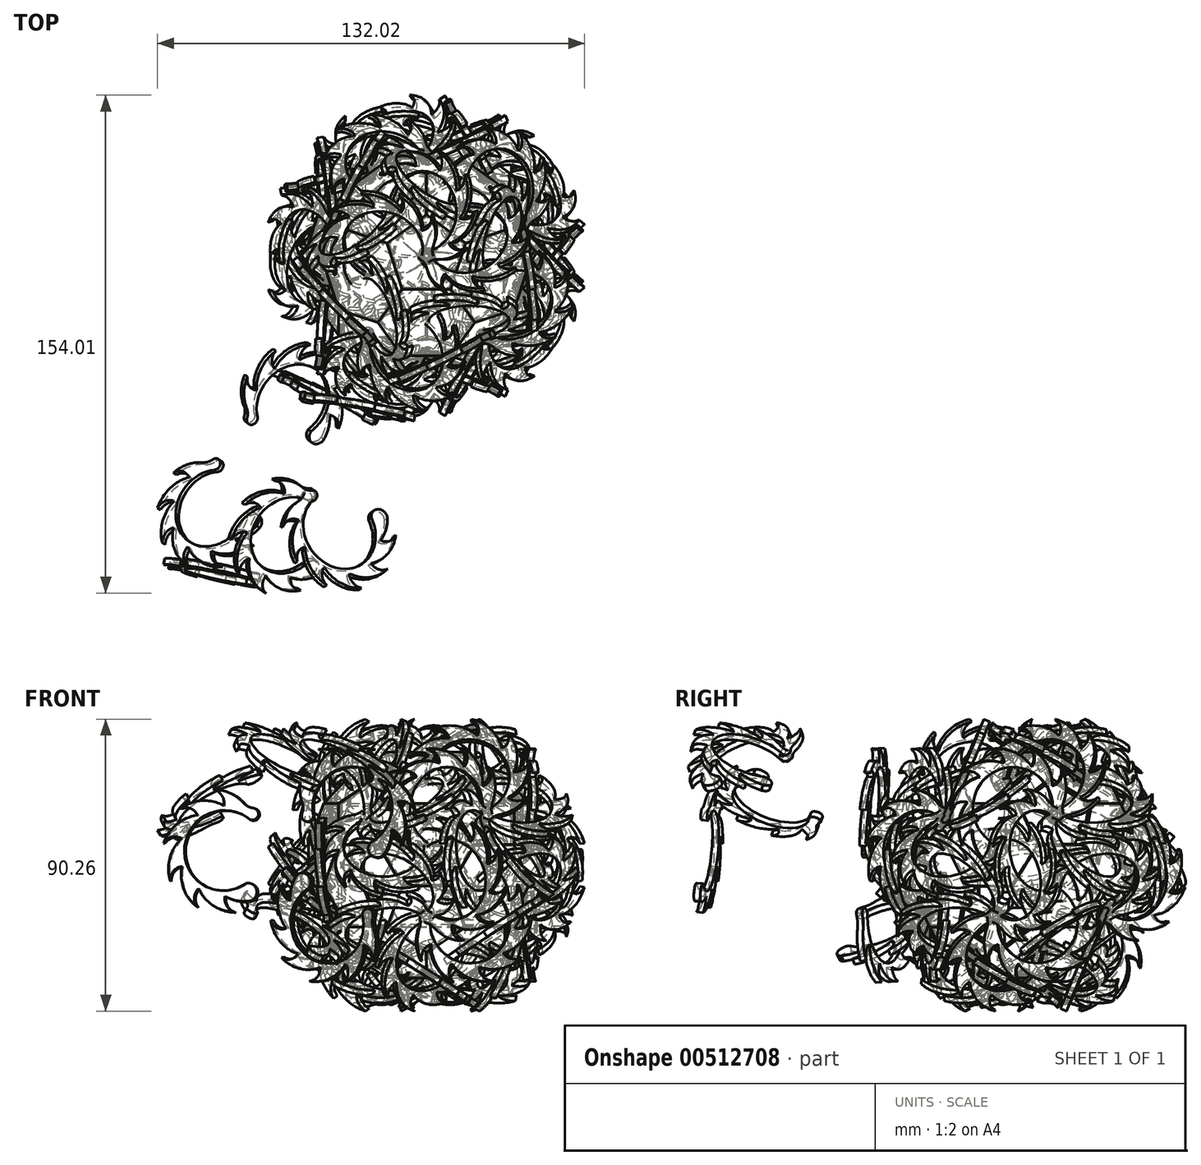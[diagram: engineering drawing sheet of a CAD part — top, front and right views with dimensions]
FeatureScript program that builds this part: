
annotation { "Feature Type Name" : "Feature", "Feature Type Description" : "" }
export const myFeature = defineFeature(function(context is Context, id is Id, definition is map)
    precondition{}
    {
        {
            var Q0;
            Q0=qCreatedBy(makeId("Top.planeOp"),FACE);
            var sketch = newSketch(context, id + "F0", { "sketchPlane" : qUnion([Q0])});
            skCircle(sketch, "E0.cCircle", {"center": v(0, 0) * mm, "radius": 10.32 * mm, "construction": true});
            skLineSegment(sketch, "E0.0", {"start": v(7.5, -10.32) * mm, "end": v(-7.5, -10.32) * mm});
            skLineSegment(sketch, "E0.1", {"start": v(-7.5, -10.32) * mm, "end": v(-12.14, 3.94) * mm});
            skLineSegment(sketch, "E0.2", {"start": v(-12.14, 3.94) * mm, "end": v(0, 12.76) * mm});
            skLineSegment(sketch, "E0.3", {"start": v(0, 12.76) * mm, "end": v(12.14, 3.94) * mm});
            skLineSegment(sketch, "E0.4", {"start": v(12.14, 3.94) * mm, "end": v(7.5, -10.32) * mm});
            skPoint(sketch, "E0.0.midPoint", {"position": v(0, -10.32) * mm});
            skLineSegment(sketch, "E1", {"start": v(0, 12.76) * mm, "end": v(0, -10.32) * mm});
            skSolve(sketch);
        }
        {
            var Q0;
            Q0=qCreatedBy(makeId("Top.planeOp"),FACE);
            var sketch = newSketch(context, id + "F1", { "sketchPlane" : qUnion([Q0])});
            skCircle(sketch, "E2.cCircle", {"center": v(22.17, -7.2) * mm, "radius": 13 * mm, "construction": true});
            skLineSegment(sketch, "E2.0", {"start": v(36.84, -4.09) * mm, "end": v(32.2, -18.35) * mm});
            skLineSegment(sketch, "E2.1", {"start": v(32.2, -18.35) * mm, "end": v(17.54, -21.47) * mm});
            skLineSegment(sketch, "E2.2", {"start": v(17.54, -21.47) * mm, "end": v(7.5, -10.32) * mm});
            skLineSegment(sketch, "E2.3", {"start": v(7.5, -10.32) * mm, "end": v(12.14, 3.94) * mm});
            skLineSegment(sketch, "E2.4", {"start": v(12.14, 3.94) * mm, "end": v(26.8, 7.06) * mm});
            skLineSegment(sketch, "E2.5", {"start": v(26.8, 7.06) * mm, "end": v(36.84, -4.09) * mm});
            skPoint(sketch, "E2.0.midPoint", {"position": v(34.53, -11.22) * mm});
            skSolve(sketch);
        }
        {
            var Q0;
            Q0=makeQuery(id+"F0.imprint","IMPRINT",FACE,{"disambiguationData":[TD([[makeQuery(id+"F0.imprint","IMPRINT",EDGE,{"derivedFrom":sQuery(id+"F0.wireOp",EDGE,"E0.0")}),-1.0]])]});
            extrude(context, id + "F2", {"entities" : qUnion([Q0]), "oppositeDirection" : true, "depth" : 1 * mm});
        }
        {
            var Q0;
            Q0=makeQuery(id+"F1.imprint","IMPRINT",FACE,{"disambiguationData":[TD([[makeQuery(id+"F1.imprint","IMPRINT",EDGE,{"derivedFrom":sQuery(id+"F1.wireOp",EDGE,"E2.0")}),-1.0]])]});
            extrude(context, id + "F3", {"entities" : qUnion([Q0]), "oppositeDirection" : true, "depth" : 1 * mm});
        }
        {
            var Q0;
            Q0=makeQuery(id+"F3.opExtrude","SWEPT_BODY",BODY,{"disambiguationData":[OSD([sQuery(id+"F1.wireOp",EDGE,"E2.0"),sQuery(id+"F1.wireOp",EDGE,"E2.1"),sQuery(id+"F1.wireOp",EDGE,"E2.2"),sQuery(id+"F1.wireOp",EDGE,"E2.3"),sQuery(id+"F1.wireOp",EDGE,"E2.4"),sQuery(id+"F1.wireOp",EDGE,"E2.5")])]});
            var Q1;
            Q1=makeQuery(id+"F2.opExtrude","CAP_EDGE",EDGE,{"disambiguationData":[OSD([sQuery(id+"F0.wireOp",EDGE,"E0.4")])],"isStart":true});
            transform(context, id + "F4", {"entities" : qUnion([Q0]), "transformType" : TransformType.ROTATION, "transformAxis" : qUnion([Q1]), "angle" : 37.38 * degree, "oppositeDirection" : true, "makeCopy" : false});
        }
        {
            var Q0;
            Q0=qCreatedBy(makeId("Right.planeOp"),FACE);
            var sketch = newSketch(context, id + "F5", { "sketchPlane" : qUnion([Q0])});
            skLineSegment(sketch, "E3", {"start": v(0, 0) * mm, "end": v(0, 7.73) * mm});
            skSolve(sketch);
        }
        {
            var Q0;
            Q0=makeQuery(id+"F3.opExtrude","SWEPT_BODY",BODY,{"disambiguationData":[OSD([sQuery(id+"F1.wireOp",EDGE,"E2.0"),sQuery(id+"F1.wireOp",EDGE,"E2.1"),sQuery(id+"F1.wireOp",EDGE,"E2.2"),sQuery(id+"F1.wireOp",EDGE,"E2.3"),sQuery(id+"F1.wireOp",EDGE,"E2.4"),sQuery(id+"F1.wireOp",EDGE,"E2.5")])]});
            var Q1;
            Q1=sQuery(id+"F5.wireOp",EDGE,"E3");
            circularPattern(context, id + "F6", {"entities" : qUnion([Q0]), "axis" : qUnion([Q1]), "angle" : 72 * degree, "instanceCount" : round(5)});
        }
        {
            var Q0;
            Q0=makeQuery(id+"F6.opPattern","COPY",FACE,{"derivedFrom":makeQuery(id+"F3.opExtrude","CAP_FACE",FACE,{"disambiguationData":[OSD([sQuery(id+"F1.wireOp",EDGE,"E2.0"),sQuery(id+"F1.wireOp",EDGE,"E2.1"),sQuery(id+"F1.wireOp",EDGE,"E2.2"),sQuery(id+"F1.wireOp",EDGE,"E2.3"),sQuery(id+"F1.wireOp",EDGE,"E2.4"),sQuery(id+"F1.wireOp",EDGE,"E2.5")])],"isStart":true}),"instanceName":"4"});
            var sketch = newSketch(context, id + "F7", { "sketchPlane" : qUnion([Q0])});
            skLineSegment(sketch, "E4", {"start": v(0, -34.18) * mm, "end": v(0, -8.2) * mm});
            skLineSegment(sketch, "E5", {"start": v(-15, -21.2) * mm, "end": v(15, -21.2) * mm});
            skCircle(sketch, "E6", {"center": v(0, -21.2) * mm, "radius": 3.24 * mm});
            skSolve(sketch);
        }
        {
            var Q0;
            Q0=qCreatedBy(makeId("Right.planeOp"),FACE);
            var sketch = newSketch(context, id + "F8", { "sketchPlane" : qUnion([Q0])});
            skArc(sketch, "E7.0", {"start": v(-1.37, 0) * mm, "mid": v(-18.04, 14.75) * mm, "end": v(-20.04, -7.42) * mm});
            skLineSegment(sketch, "E8", {"start": v(-20.04, -7.42) * mm, "end": v(-24.47, -10.8) * mm});
            skLineSegment(sketch, "E9", {"start": v(-1.37, 0) * mm, "end": v(0, 0) * mm});
            skArc(sketch, "E10", {"start": v(1.07, 1.27) * mm, "mid": v(3.46, 7.37) * mm, "end": v(2.5, 13.85) * mm});
            skArc(sketch, "E11", {"start": v(-0.8, 8.97) * mm, "mid": v(1.84, 10.74) * mm, "end": v(2.5, 13.85) * mm});
            skArc(sketch, "E12.1.0", {"start": v(-0.8, 8.97) * mm, "mid": v(-2.13, 15.94) * mm, "end": v(-6.98, 21.1) * mm});
            skArc(sketch, "E12.1.1", {"start": v(-6.75, 15.32) * mm, "mid": v(-5.72, 18.26) * mm, "end": v(-6.98, 21.1) * mm});
            skArc(sketch, "E12.2.0", {"start": v(-6.75, 15.32) * mm, "mid": v(-11.92, 20.18) * mm, "end": v(-18.89, 21.5) * mm});
            skArc(sketch, "E12.2.1", {"start": v(-15.3, 16.96) * mm, "mid": v(-16.2, 19.94) * mm, "end": v(-18.89, 21.5) * mm});
            skArc(sketch, "E12.3.0", {"start": v(-15.3, 16.96) * mm, "mid": v(-22.34, 17.85) * mm, "end": v(-28.75, 14.83) * mm});
            skArc(sketch, "E12.3.1", {"start": v(-23.18, 13.26) * mm, "mid": v(-25.66, 15.15) * mm, "end": v(-28.75, 14.83) * mm});
            skArc(sketch, "E12.4.0", {"start": v(-23.18, 13.26) * mm, "mid": v(-29.4, 9.84) * mm, "end": v(-32.81, 3.63) * mm});
            skArc(sketch, "E12.4.1", {"start": v(-27.38, 5.64) * mm, "mid": v(-30.5, 5.7) * mm, "end": v(-32.81, 3.63) * mm});
            skArc(sketch, "E12.5.0", {"start": v(-27.38, 5.64) * mm, "mid": v(-30.4, -0.78) * mm, "end": v(-29.51, -7.81) * mm});
            skArc(sketch, "E12.5.1", {"start": v(-26.3, -3) * mm, "mid": v(-28.86, -4.77) * mm, "end": v(-29.51, -7.81) * mm});
            skArc(sketch, "E12.6.0", {"start": v(-26.3, -3) * mm, "mid": v(-26.03, -7.06) * mm, "end": v(-24.49, -10.82) * mm});
            skArc(sketch, "E13", {"start": v(-24.49, -10.82) * mm, "mid": v(-20.56, -11.35) * mm, "end": v(-20.04, -7.42) * mm});
            skArc(sketch, "E14", {"start": v(-1.37, 0) * mm, "mid": v(1.27, -2.11) * mm, "end": v(1.07, 1.27) * mm});
            skSolve(sketch);
        }
        {
            var Q0;
            {var subQ2=sQuery(id+"F8.wireOp",EDGE,"E7.0");Q0=makeQuery(id+"F8.imprint","IMPRINT",FACE,{"disambiguationData":[TD([[makeQuery(id+"F8.imprint","IMPRINT",EDGE,{"derivedFrom":subQ2}),-1.0]])]});}
            extrude(context, id + "F9", {"entities" : qUnion([Q0]), "oppositeDirection" : true, "depth" : 2 * mm});
        }
        {
            var Q0;
            Q0=makeQuery(id+"F9.opExtrude","SWEPT_EDGE",EDGE,{"disambiguationData":[OSD([sQuery(id+"F8.wireOp",EDGE,"E10"),sQuery(id+"F8.wireOp",EDGE,"E14")])]});
            fillet(context, id + "F10", {"entities" : qUnion([Q0]), "radius" : 5.46 * mm, "tangentPropagation" : true, "allowEdgeOverflow" : false});
        }
        {
            var Q0;
            Q0=qCreatedBy(makeId("Right.planeOp"),FACE);
            var sketch = newSketch(context, id + "F11", { "sketchPlane" : qUnion([Q0])});
            skLineSegment(sketch, "E15", {"start": v(0, 0) * mm, "end": v(-20.65, -7.89) * mm});
            skLineSegment(sketch, "E16", {"start": v(0, 0) * mm, "end": v(0, 28.42) * mm});
            skSolve(sketch);
        }
        {
            var Q0;
            Q0=makeQuery(id+"F9.opExtrude","SWEPT_BODY",BODY,{"disambiguationData":[OSD([sQuery(id+"F8.wireOp",EDGE,"003f2e54-bd62-4f0b-a98e-8c36e71e2cf6"),sQuery(id+"F8.wireOp",EDGE,"8c729305-40a1-49fa-b790-4b99a3909bb6"),sQuery(id+"F8.wireOp",EDGE,"862a2a8f-3db7-4421-9c69-6ab2f53c4c24.1.0"),sQuery(id+"F8.wireOp",EDGE,"862a2a8f-3db7-4421-9c69-6ab2f53c4c24.1.1"),sQuery(id+"F8.wireOp",EDGE,"862a2a8f-3db7-4421-9c69-6ab2f53c4c24.2.0"),sQuery(id+"F8.wireOp",EDGE,"862a2a8f-3db7-4421-9c69-6ab2f53c4c24.2.1"),sQuery(id+"F8.wireOp",EDGE,"862a2a8f-3db7-4421-9c69-6ab2f53c4c24.3.0"),sQuery(id+"F8.wireOp",EDGE,"862a2a8f-3db7-4421-9c69-6ab2f53c4c24.3.1"),sQuery(id+"F8.wireOp",EDGE,"862a2a8f-3db7-4421-9c69-6ab2f53c4c24.4.0"),sQuery(id+"F8.wireOp",EDGE,"862a2a8f-3db7-4421-9c69-6ab2f53c4c24.4.1"),sQuery(id+"F8.wireOp",EDGE,"862a2a8f-3db7-4421-9c69-6ab2f53c4c24.5.0"),sQuery(id+"F8.wireOp",EDGE,"E7.0"),sQuery(id+"F8.wireOp",EDGE,"E8"),sQuery(id+"F8.wireOp",EDGE,"E9")])]});
            var Q1;
            Q1=sQuery(id+"F11.wireOp",EDGE,"E15");
            transform(context, id + "F12", {"entities" : qUnion([Q0]), "transformType" : TransformType.ROTATION, "transformAxis" : qUnion([Q1]), "angle" : 65 * degree, "makeCopy" : false});
        }
        {
            var Q0;
            Q0=makeQuery(id+"F9.opExtrude","SWEPT_BODY",BODY,{"disambiguationData":[OSD([sQuery(id+"F8.wireOp",EDGE,"003f2e54-bd62-4f0b-a98e-8c36e71e2cf6"),sQuery(id+"F8.wireOp",EDGE,"8c729305-40a1-49fa-b790-4b99a3909bb6"),sQuery(id+"F8.wireOp",EDGE,"862a2a8f-3db7-4421-9c69-6ab2f53c4c24.1.0"),sQuery(id+"F8.wireOp",EDGE,"862a2a8f-3db7-4421-9c69-6ab2f53c4c24.1.1"),sQuery(id+"F8.wireOp",EDGE,"862a2a8f-3db7-4421-9c69-6ab2f53c4c24.2.0"),sQuery(id+"F8.wireOp",EDGE,"862a2a8f-3db7-4421-9c69-6ab2f53c4c24.2.1"),sQuery(id+"F8.wireOp",EDGE,"862a2a8f-3db7-4421-9c69-6ab2f53c4c24.3.0"),sQuery(id+"F8.wireOp",EDGE,"862a2a8f-3db7-4421-9c69-6ab2f53c4c24.3.1"),sQuery(id+"F8.wireOp",EDGE,"862a2a8f-3db7-4421-9c69-6ab2f53c4c24.4.0"),sQuery(id+"F8.wireOp",EDGE,"862a2a8f-3db7-4421-9c69-6ab2f53c4c24.4.1"),sQuery(id+"F8.wireOp",EDGE,"862a2a8f-3db7-4421-9c69-6ab2f53c4c24.5.0"),sQuery(id+"F8.wireOp",EDGE,"E7.0"),sQuery(id+"F8.wireOp",EDGE,"E8"),sQuery(id+"F8.wireOp",EDGE,"E9")])]});
            var Q1;
            Q1=sQuery(id+"F11.wireOp",EDGE,"E16");
            circularPattern(context, id + "F13", {"entities" : qUnion([Q0]), "axis" : qUnion([Q1]), "angle" : 72 * degree, "instanceCount" : round(5)});
        }
        {
            var Q0;
            Q0=qCreatedBy(makeId("Right.planeOp"),FACE);
            var sketch = newSketch(context, id + "F14", { "sketchPlane" : qUnion([Q0])});
            skLineSegment(sketch, "E17.0", {"start": v(-30.97, -15.77) * mm, "end": v(-10.32, 0) * mm});
            skLineSegment(sketch, "E18", {"start": v(-20.65, -7.89) * mm, "end": v(-30.05, 4.42) * mm});
            skSolve(sketch);
        }
        {
            var Q0;
            Q0=makeQuery(id+"F9.opExtrude","SWEPT_BODY",BODY,{"disambiguationData":[OSD([sQuery(id+"F8.wireOp",EDGE,"003f2e54-bd62-4f0b-a98e-8c36e71e2cf6"),sQuery(id+"F8.wireOp",EDGE,"8c729305-40a1-49fa-b790-4b99a3909bb6"),sQuery(id+"F8.wireOp",EDGE,"862a2a8f-3db7-4421-9c69-6ab2f53c4c24.1.0"),sQuery(id+"F8.wireOp",EDGE,"862a2a8f-3db7-4421-9c69-6ab2f53c4c24.1.1"),sQuery(id+"F8.wireOp",EDGE,"862a2a8f-3db7-4421-9c69-6ab2f53c4c24.2.0"),sQuery(id+"F8.wireOp",EDGE,"862a2a8f-3db7-4421-9c69-6ab2f53c4c24.2.1"),sQuery(id+"F8.wireOp",EDGE,"862a2a8f-3db7-4421-9c69-6ab2f53c4c24.3.0"),sQuery(id+"F8.wireOp",EDGE,"862a2a8f-3db7-4421-9c69-6ab2f53c4c24.3.1"),sQuery(id+"F8.wireOp",EDGE,"862a2a8f-3db7-4421-9c69-6ab2f53c4c24.4.0"),sQuery(id+"F8.wireOp",EDGE,"862a2a8f-3db7-4421-9c69-6ab2f53c4c24.4.1"),sQuery(id+"F8.wireOp",EDGE,"862a2a8f-3db7-4421-9c69-6ab2f53c4c24.5.0"),sQuery(id+"F8.wireOp",EDGE,"E7.0"),sQuery(id+"F8.wireOp",EDGE,"E8"),sQuery(id+"F8.wireOp",EDGE,"E9")])]});
            var Q1;
            Q1=sQuery(id+"F14.wireOp",EDGE,"E18");
            circularPattern(context, id + "F15", {"entities" : qUnion([Q0]), "axis" : qUnion([Q1]), "angle" : 120 * degree, "instanceCount" : round(3)});
        }
        {
            var Q0;
            Q0=makeQuery(id+"F15.opPattern","COPY",BODY,{"derivedFrom":makeQuery(id+"F9.opExtrude","SWEPT_BODY",BODY,{"disambiguationData":[OSD([sQuery(id+"F8.wireOp",EDGE,"E7.0"),sQuery(id+"F8.wireOp",EDGE,"E10"),sQuery(id+"F8.wireOp",EDGE,"E11"),sQuery(id+"F8.wireOp",EDGE,"E12.1.0"),sQuery(id+"F8.wireOp",EDGE,"E12.1.1"),sQuery(id+"F8.wireOp",EDGE,"E12.2.0"),sQuery(id+"F8.wireOp",EDGE,"E12.2.1"),sQuery(id+"F8.wireOp",EDGE,"E12.3.0"),sQuery(id+"F8.wireOp",EDGE,"E12.3.1"),sQuery(id+"F8.wireOp",EDGE,"E12.4.0"),sQuery(id+"F8.wireOp",EDGE,"E12.4.1"),sQuery(id+"F8.wireOp",EDGE,"E12.5.0"),sQuery(id+"F8.wireOp",EDGE,"E12.5.1"),sQuery(id+"F8.wireOp",EDGE,"E12.6.0"),sQuery(id+"F8.wireOp",EDGE,"E13"),sQuery(id+"F8.wireOp",EDGE,"E14")])]}),"instanceName":"2"});
            var Q1;
            Q1=makeQuery(id+"F15.opPattern","COPY",BODY,{"derivedFrom":makeQuery(id+"F9.opExtrude","SWEPT_BODY",BODY,{"disambiguationData":[OSD([sQuery(id+"F8.wireOp",EDGE,"E7.0"),sQuery(id+"F8.wireOp",EDGE,"E10"),sQuery(id+"F8.wireOp",EDGE,"E11"),sQuery(id+"F8.wireOp",EDGE,"E12.1.0"),sQuery(id+"F8.wireOp",EDGE,"E12.1.1"),sQuery(id+"F8.wireOp",EDGE,"E12.2.0"),sQuery(id+"F8.wireOp",EDGE,"E12.2.1"),sQuery(id+"F8.wireOp",EDGE,"E12.3.0"),sQuery(id+"F8.wireOp",EDGE,"E12.3.1"),sQuery(id+"F8.wireOp",EDGE,"E12.4.0"),sQuery(id+"F8.wireOp",EDGE,"E12.4.1"),sQuery(id+"F8.wireOp",EDGE,"E12.5.0"),sQuery(id+"F8.wireOp",EDGE,"E12.5.1"),sQuery(id+"F8.wireOp",EDGE,"E12.6.0"),sQuery(id+"F8.wireOp",EDGE,"E13"),sQuery(id+"F8.wireOp",EDGE,"E14")])]}),"instanceName":"1"});
            var Q2;
            Q2=sQuery(id+"F11.wireOp",EDGE,"E16");
            circularPattern(context, id + "F16", {"entities" : qUnion([Q0, Q1]), "axis" : qUnion([Q2]), "angle" : 72 * degree, "instanceCount" : round(5)});
        }
        {
            var Q0;
            Q0=makeQuery(id+"F3.opExtrude","SWEPT_BODY",BODY,{"disambiguationData":[OSD([sQuery(id+"F1.wireOp",EDGE,"E2.0"),sQuery(id+"F1.wireOp",EDGE,"E2.1"),sQuery(id+"F1.wireOp",EDGE,"E2.2"),sQuery(id+"F1.wireOp",EDGE,"E2.3"),sQuery(id+"F1.wireOp",EDGE,"E2.4"),sQuery(id+"F1.wireOp",EDGE,"E2.5")])]});
            var Q1;
            Q1=makeQuery(id+"F16.opPattern","COPY",BODY,{"derivedFrom":makeQuery(id+"F15.opPattern","COPY",BODY,{"derivedFrom":makeQuery(id+"F9.opExtrude","SWEPT_BODY",BODY,{"disambiguationData":[OSD([sQuery(id+"F8.wireOp",EDGE,"E7.0"),sQuery(id+"F8.wireOp",EDGE,"E10"),sQuery(id+"F8.wireOp",EDGE,"E11"),sQuery(id+"F8.wireOp",EDGE,"E12.1.0"),sQuery(id+"F8.wireOp",EDGE,"E12.1.1"),sQuery(id+"F8.wireOp",EDGE,"E12.2.0"),sQuery(id+"F8.wireOp",EDGE,"E12.2.1"),sQuery(id+"F8.wireOp",EDGE,"E12.3.0"),sQuery(id+"F8.wireOp",EDGE,"E12.3.1"),sQuery(id+"F8.wireOp",EDGE,"E12.4.0"),sQuery(id+"F8.wireOp",EDGE,"E12.4.1"),sQuery(id+"F8.wireOp",EDGE,"E12.5.0"),sQuery(id+"F8.wireOp",EDGE,"E12.5.1"),sQuery(id+"F8.wireOp",EDGE,"E12.6.0"),sQuery(id+"F8.wireOp",EDGE,"E13"),sQuery(id+"F8.wireOp",EDGE,"E14")])]}),"instanceName":"1"}),"instanceName":"1"});
            var Q2;
            Q2=makeQuery(id+"F13.opPattern","COPY",BODY,{"derivedFrom":makeQuery(id+"F9.opExtrude","SWEPT_BODY",BODY,{"disambiguationData":[OSD([sQuery(id+"F8.wireOp",EDGE,"E7.0"),sQuery(id+"F8.wireOp",EDGE,"E10"),sQuery(id+"F8.wireOp",EDGE,"E11"),sQuery(id+"F8.wireOp",EDGE,"E12.1.0"),sQuery(id+"F8.wireOp",EDGE,"E12.1.1"),sQuery(id+"F8.wireOp",EDGE,"E12.2.0"),sQuery(id+"F8.wireOp",EDGE,"E12.2.1"),sQuery(id+"F8.wireOp",EDGE,"E12.3.0"),sQuery(id+"F8.wireOp",EDGE,"E12.3.1"),sQuery(id+"F8.wireOp",EDGE,"E12.4.0"),sQuery(id+"F8.wireOp",EDGE,"E12.4.1"),sQuery(id+"F8.wireOp",EDGE,"E12.5.0"),sQuery(id+"F8.wireOp",EDGE,"E12.5.1"),sQuery(id+"F8.wireOp",EDGE,"E12.6.0"),sQuery(id+"F8.wireOp",EDGE,"E13"),sQuery(id+"F8.wireOp",EDGE,"E14")])]}),"instanceName":"1"});
            var Q3;
            Q3=makeQuery(id+"F16.opPattern","COPY",BODY,{"derivedFrom":makeQuery(id+"F15.opPattern","COPY",BODY,{"derivedFrom":makeQuery(id+"F9.opExtrude","SWEPT_BODY",BODY,{"disambiguationData":[OSD([sQuery(id+"F8.wireOp",EDGE,"E7.0"),sQuery(id+"F8.wireOp",EDGE,"E10"),sQuery(id+"F8.wireOp",EDGE,"E11"),sQuery(id+"F8.wireOp",EDGE,"E12.1.0"),sQuery(id+"F8.wireOp",EDGE,"E12.1.1"),sQuery(id+"F8.wireOp",EDGE,"E12.2.0"),sQuery(id+"F8.wireOp",EDGE,"E12.2.1"),sQuery(id+"F8.wireOp",EDGE,"E12.3.0"),sQuery(id+"F8.wireOp",EDGE,"E12.3.1"),sQuery(id+"F8.wireOp",EDGE,"E12.4.0"),sQuery(id+"F8.wireOp",EDGE,"E12.4.1"),sQuery(id+"F8.wireOp",EDGE,"E12.5.0"),sQuery(id+"F8.wireOp",EDGE,"E12.5.1"),sQuery(id+"F8.wireOp",EDGE,"E12.6.0"),sQuery(id+"F8.wireOp",EDGE,"E13"),sQuery(id+"F8.wireOp",EDGE,"E14")])]}),"instanceName":"2"}),"instanceName":"1"});
            var Q4;
            Q4=sQuery(id+"F14.wireOp",EDGE,"E18");
            circularPattern(context, id + "F17", {"entities" : qUnion([Q0, Q1, Q2, Q3]), "axis" : qUnion([Q4]), "angle" : 120 * degree, "instanceCount" : 2, "oppositeDirection" : true});
        }
        {
            var Q0;
            Q0=makeQuery(id+"F2.opExtrude","SWEPT_BODY",BODY,{"disambiguationData":[OSD([sQuery(id+"F0.wireOp",EDGE,"E0.0"),sQuery(id+"F0.wireOp",EDGE,"E0.1"),sQuery(id+"F0.wireOp",EDGE,"E0.2"),sQuery(id+"F0.wireOp",EDGE,"E0.3"),sQuery(id+"F0.wireOp",EDGE,"E0.4")])]});
            var Q1;
            Q1=makeQuery(id+"F13.opPattern","COPY",BODY,{"derivedFrom":makeQuery(id+"F9.opExtrude","SWEPT_BODY",BODY,{"disambiguationData":[OSD([sQuery(id+"F8.wireOp",EDGE,"E7.0"),sQuery(id+"F8.wireOp",EDGE,"E10"),sQuery(id+"F8.wireOp",EDGE,"E11"),sQuery(id+"F8.wireOp",EDGE,"E12.1.0"),sQuery(id+"F8.wireOp",EDGE,"E12.1.1"),sQuery(id+"F8.wireOp",EDGE,"E12.2.0"),sQuery(id+"F8.wireOp",EDGE,"E12.2.1"),sQuery(id+"F8.wireOp",EDGE,"E12.3.0"),sQuery(id+"F8.wireOp",EDGE,"E12.3.1"),sQuery(id+"F8.wireOp",EDGE,"E12.4.0"),sQuery(id+"F8.wireOp",EDGE,"E12.4.1"),sQuery(id+"F8.wireOp",EDGE,"E12.5.0"),sQuery(id+"F8.wireOp",EDGE,"E12.5.1"),sQuery(id+"F8.wireOp",EDGE,"E12.6.0"),sQuery(id+"F8.wireOp",EDGE,"E13"),sQuery(id+"F8.wireOp",EDGE,"E14")])]}),"instanceName":"2"});
            var Q2;
            Q2=makeQuery(id+"F13.opPattern","COPY",BODY,{"derivedFrom":makeQuery(id+"F9.opExtrude","SWEPT_BODY",BODY,{"disambiguationData":[OSD([sQuery(id+"F8.wireOp",EDGE,"E7.0"),sQuery(id+"F8.wireOp",EDGE,"E10"),sQuery(id+"F8.wireOp",EDGE,"E11"),sQuery(id+"F8.wireOp",EDGE,"E12.1.0"),sQuery(id+"F8.wireOp",EDGE,"E12.1.1"),sQuery(id+"F8.wireOp",EDGE,"E12.2.0"),sQuery(id+"F8.wireOp",EDGE,"E12.2.1"),sQuery(id+"F8.wireOp",EDGE,"E12.3.0"),sQuery(id+"F8.wireOp",EDGE,"E12.3.1"),sQuery(id+"F8.wireOp",EDGE,"E12.4.0"),sQuery(id+"F8.wireOp",EDGE,"E12.4.1"),sQuery(id+"F8.wireOp",EDGE,"E12.5.0"),sQuery(id+"F8.wireOp",EDGE,"E12.5.1"),sQuery(id+"F8.wireOp",EDGE,"E12.6.0"),sQuery(id+"F8.wireOp",EDGE,"E13"),sQuery(id+"F8.wireOp",EDGE,"E14")])]}),"instanceName":"3"});
            var Q3;
            Q3=sQuery(id+"F14.wireOp",EDGE,"E18");
            circularPattern(context, id + "F18", {"entities" : qUnion([Q0, Q1, Q2]), "axis" : qUnion([Q3]), "angle" : 120 * degree, "instanceCount" : round(3)});
        }
        {
            var Q0;
            Q0=makeQuery(id+"F18.opPattern","COPY",FACE,{"derivedFrom":makeQuery(id+"F2.opExtrude","CAP_FACE",FACE,{"disambiguationData":[OSD([sQuery(id+"F0.wireOp",EDGE,"E0.0"),sQuery(id+"F0.wireOp",EDGE,"E0.1"),sQuery(id+"F0.wireOp",EDGE,"E0.2"),sQuery(id+"F0.wireOp",EDGE,"E0.3"),sQuery(id+"F0.wireOp",EDGE,"E0.4")])],"isStart":true}),"instanceName":"1"});
            var sketch = newSketch(context, id + "F19", { "sketchPlane" : qUnion([Q0])});
            skLineSegment(sketch, "E19", {"start": v(-1.3, -23.63) * mm, "end": v(-19.97, -37.2) * mm});
            skLineSegment(sketch, "E20", {"start": v(-19.97, -22.2) * mm, "end": v(-1.3, -35.77) * mm});
            skSolve(sketch);
        }
        {
            var Q0;
            Q0=sQuery(id+"F19.wireOp",VERTEX,"E19.end");
            var Q1;
            Q1=sQuery(id+"F19.wireOp",VERTEX,"E19.start");
            var Q2;
            Q2=sQuery(id+"F14.wireOp",VERTEX,"E18.end");
            cPlane(context, id + "F20", {"entities" : qUnion([Q0, Q1, Q2]), "cplaneType" : CPlaneType.THREE_POINT, "offset" : 150 * mm, "width" : 150 * mm, "height" : 150 * mm});
        }
        {
            var Q0;
            Q0=qCreatedBy(id+"F20.planeOp",FACE);
            var sketch = newSketch(context, id + "F21", { "sketchPlane" : qUnion([Q0])});
            skLineSegment(sketch, "E21.0", {"start": v(23.59, 6.27) * mm, "end": v(41.93, -7.75) * mm});
            skLineSegment(sketch, "E21.1", {"start": v(34.92, -2.4) * mm, "end": v(29.26, 1.94) * mm});
            skLineSegment(sketch, "E22", {"start": v(31.8, 0) * mm, "end": v(33.22, 1.87) * mm});
            skLineSegment(sketch, "E23", {"start": v(33.22, 1.87) * mm, "end": v(37.58, 7.58) * mm});
            skSolve(sketch);
        }
        {
            var Q0;
            Q0=makeQuery(id+"F17.opPattern","COPY",BODY,{"derivedFrom":makeQuery(id+"F3.opExtrude","SWEPT_BODY",BODY,{"disambiguationData":[OSD([sQuery(id+"F1.wireOp",EDGE,"E2.0"),sQuery(id+"F1.wireOp",EDGE,"E2.1"),sQuery(id+"F1.wireOp",EDGE,"E2.2"),sQuery(id+"F1.wireOp",EDGE,"E2.3"),sQuery(id+"F1.wireOp",EDGE,"E2.4"),sQuery(id+"F1.wireOp",EDGE,"E2.5")])]}),"instanceName":"1"});
            var Q1;
            Q1=makeQuery(id+"F17.opPattern","COPY",BODY,{"derivedFrom":makeQuery(id+"F13.opPattern","COPY",BODY,{"derivedFrom":makeQuery(id+"F9.opExtrude","SWEPT_BODY",BODY,{"disambiguationData":[OSD([sQuery(id+"F8.wireOp",EDGE,"E7.0"),sQuery(id+"F8.wireOp",EDGE,"E10"),sQuery(id+"F8.wireOp",EDGE,"E11"),sQuery(id+"F8.wireOp",EDGE,"E12.1.0"),sQuery(id+"F8.wireOp",EDGE,"E12.1.1"),sQuery(id+"F8.wireOp",EDGE,"E12.2.0"),sQuery(id+"F8.wireOp",EDGE,"E12.2.1"),sQuery(id+"F8.wireOp",EDGE,"E12.3.0"),sQuery(id+"F8.wireOp",EDGE,"E12.3.1"),sQuery(id+"F8.wireOp",EDGE,"E12.4.0"),sQuery(id+"F8.wireOp",EDGE,"E12.4.1"),sQuery(id+"F8.wireOp",EDGE,"E12.5.0"),sQuery(id+"F8.wireOp",EDGE,"E12.5.1"),sQuery(id+"F8.wireOp",EDGE,"E12.6.0"),sQuery(id+"F8.wireOp",EDGE,"E13"),sQuery(id+"F8.wireOp",EDGE,"E14")])]}),"instanceName":"1"}),"instanceName":"1"});
            var Q2;
            Q2=makeQuery(id+"F17.opPattern","COPY",BODY,{"derivedFrom":makeQuery(id+"F16.opPattern","COPY",BODY,{"derivedFrom":makeQuery(id+"F15.opPattern","COPY",BODY,{"derivedFrom":makeQuery(id+"F9.opExtrude","SWEPT_BODY",BODY,{"disambiguationData":[OSD([sQuery(id+"F8.wireOp",EDGE,"E7.0"),sQuery(id+"F8.wireOp",EDGE,"E10"),sQuery(id+"F8.wireOp",EDGE,"E11"),sQuery(id+"F8.wireOp",EDGE,"E12.1.0"),sQuery(id+"F8.wireOp",EDGE,"E12.1.1"),sQuery(id+"F8.wireOp",EDGE,"E12.2.0"),sQuery(id+"F8.wireOp",EDGE,"E12.2.1"),sQuery(id+"F8.wireOp",EDGE,"E12.3.0"),sQuery(id+"F8.wireOp",EDGE,"E12.3.1"),sQuery(id+"F8.wireOp",EDGE,"E12.4.0"),sQuery(id+"F8.wireOp",EDGE,"E12.4.1"),sQuery(id+"F8.wireOp",EDGE,"E12.5.0"),sQuery(id+"F8.wireOp",EDGE,"E12.5.1"),sQuery(id+"F8.wireOp",EDGE,"E12.6.0"),sQuery(id+"F8.wireOp",EDGE,"E13"),sQuery(id+"F8.wireOp",EDGE,"E14")])]}),"instanceName":"2"}),"instanceName":"1"}),"instanceName":"1"});
            var Q3;
            Q3=makeQuery(id+"F17.opPattern","COPY",BODY,{"derivedFrom":makeQuery(id+"F16.opPattern","COPY",BODY,{"derivedFrom":makeQuery(id+"F15.opPattern","COPY",BODY,{"derivedFrom":makeQuery(id+"F9.opExtrude","SWEPT_BODY",BODY,{"disambiguationData":[OSD([sQuery(id+"F8.wireOp",EDGE,"E7.0"),sQuery(id+"F8.wireOp",EDGE,"E10"),sQuery(id+"F8.wireOp",EDGE,"E11"),sQuery(id+"F8.wireOp",EDGE,"E12.1.0"),sQuery(id+"F8.wireOp",EDGE,"E12.1.1"),sQuery(id+"F8.wireOp",EDGE,"E12.2.0"),sQuery(id+"F8.wireOp",EDGE,"E12.2.1"),sQuery(id+"F8.wireOp",EDGE,"E12.3.0"),sQuery(id+"F8.wireOp",EDGE,"E12.3.1"),sQuery(id+"F8.wireOp",EDGE,"E12.4.0"),sQuery(id+"F8.wireOp",EDGE,"E12.4.1"),sQuery(id+"F8.wireOp",EDGE,"E12.5.0"),sQuery(id+"F8.wireOp",EDGE,"E12.5.1"),sQuery(id+"F8.wireOp",EDGE,"E12.6.0"),sQuery(id+"F8.wireOp",EDGE,"E13"),sQuery(id+"F8.wireOp",EDGE,"E14")])]}),"instanceName":"1"}),"instanceName":"1"}),"instanceName":"1"});
            var Q4;
            Q4=sQuery(id+"F21.wireOp",EDGE,"E22");
            circularPattern(context, id + "F22", {"entities" : qUnion([Q0, Q1, Q2, Q3]), "axis" : qUnion([Q4]), "angle" : 72 * degree, "instanceCount" : round(3), "oppositeDirection" : true});
        }
        {
            var Q0;
            Q0=makeQuery(id+"F18.opPattern","COPY",FACE,{"derivedFrom":makeQuery(id+"F2.opExtrude","CAP_FACE",FACE,{"disambiguationData":[OSD([sQuery(id+"F0.wireOp",EDGE,"E0.0"),sQuery(id+"F0.wireOp",EDGE,"E0.1"),sQuery(id+"F0.wireOp",EDGE,"E0.2"),sQuery(id+"F0.wireOp",EDGE,"E0.3"),sQuery(id+"F0.wireOp",EDGE,"E0.4")])],"isStart":true}),"instanceName":"2"});
            var sketch = newSketch(context, id + "F23", { "sketchPlane" : qUnion([Q0])});
            skLineSegment(sketch, "E24", {"start": v(1.3, -23.63) * mm, "end": v(19.97, -37.2) * mm});
            skLineSegment(sketch, "E25", {"start": v(5.7, -41.83) * mm, "end": v(12.84, -19.88) * mm});
            skSolve(sketch);
        }
        {
            var Q0;
            Q0=sQuery(id+"F23.wireOp",VERTEX,"E24.end");
            var Q1;
            Q1=sQuery(id+"F23.wireOp",VERTEX,"E24.start");
            var Q2;
            Q2=sQuery(id+"F14.wireOp",VERTEX,"E18.end");
            cPlane(context, id + "F24", {"entities" : qUnion([Q0, Q1, Q2]), "cplaneType" : CPlaneType.THREE_POINT, "offset" : 150 * mm, "width" : 150 * mm, "height" : 150 * mm});
        }
        {
            var Q0;
            Q0=qCreatedBy(id+"F24.planeOp",FACE);
            var sketch = newSketch(context, id + "F25", { "sketchPlane" : qUnion([Q0])});
            skLineSegment(sketch, "E26.0", {"start": v(23.59, 6.27) * mm, "end": v(41.93, -7.75) * mm});
            skLineSegment(sketch, "E26.1", {"start": v(34.92, -2.4) * mm, "end": v(29.26, 1.94) * mm});
            skLineSegment(sketch, "E27", {"start": v(31.8, 0) * mm, "end": v(36.23, 5.8) * mm});
            skSolve(sketch);
        }
        {
            var Q0;
            Q0=makeQuery(id+"F3.opExtrude","SWEPT_BODY",BODY,{"disambiguationData":[OSD([sQuery(id+"F1.wireOp",EDGE,"E2.0"),sQuery(id+"F1.wireOp",EDGE,"E2.1"),sQuery(id+"F1.wireOp",EDGE,"E2.2"),sQuery(id+"F1.wireOp",EDGE,"E2.3"),sQuery(id+"F1.wireOp",EDGE,"E2.4"),sQuery(id+"F1.wireOp",EDGE,"E2.5")])]});
            var Q1;
            Q1=makeQuery(id+"F16.opPattern","COPY",BODY,{"derivedFrom":makeQuery(id+"F15.opPattern","COPY",BODY,{"derivedFrom":makeQuery(id+"F9.opExtrude","SWEPT_BODY",BODY,{"disambiguationData":[OSD([sQuery(id+"F8.wireOp",EDGE,"E7.0"),sQuery(id+"F8.wireOp",EDGE,"E10"),sQuery(id+"F8.wireOp",EDGE,"E11"),sQuery(id+"F8.wireOp",EDGE,"E12.1.0"),sQuery(id+"F8.wireOp",EDGE,"E12.1.1"),sQuery(id+"F8.wireOp",EDGE,"E12.2.0"),sQuery(id+"F8.wireOp",EDGE,"E12.2.1"),sQuery(id+"F8.wireOp",EDGE,"E12.3.0"),sQuery(id+"F8.wireOp",EDGE,"E12.3.1"),sQuery(id+"F8.wireOp",EDGE,"E12.4.0"),sQuery(id+"F8.wireOp",EDGE,"E12.4.1"),sQuery(id+"F8.wireOp",EDGE,"E12.5.0"),sQuery(id+"F8.wireOp",EDGE,"E12.5.1"),sQuery(id+"F8.wireOp",EDGE,"E12.6.0"),sQuery(id+"F8.wireOp",EDGE,"E13"),sQuery(id+"F8.wireOp",EDGE,"E14")])]}),"instanceName":"2"}),"instanceName":"1"});
            var Q2;
            Q2=makeQuery(id+"F13.opPattern","COPY",BODY,{"derivedFrom":makeQuery(id+"F9.opExtrude","SWEPT_BODY",BODY,{"disambiguationData":[OSD([sQuery(id+"F8.wireOp",EDGE,"E7.0"),sQuery(id+"F8.wireOp",EDGE,"E10"),sQuery(id+"F8.wireOp",EDGE,"E11"),sQuery(id+"F8.wireOp",EDGE,"E12.1.0"),sQuery(id+"F8.wireOp",EDGE,"E12.1.1"),sQuery(id+"F8.wireOp",EDGE,"E12.2.0"),sQuery(id+"F8.wireOp",EDGE,"E12.2.1"),sQuery(id+"F8.wireOp",EDGE,"E12.3.0"),sQuery(id+"F8.wireOp",EDGE,"E12.3.1"),sQuery(id+"F8.wireOp",EDGE,"E12.4.0"),sQuery(id+"F8.wireOp",EDGE,"E12.4.1"),sQuery(id+"F8.wireOp",EDGE,"E12.5.0"),sQuery(id+"F8.wireOp",EDGE,"E12.5.1"),sQuery(id+"F8.wireOp",EDGE,"E12.6.0"),sQuery(id+"F8.wireOp",EDGE,"E13"),sQuery(id+"F8.wireOp",EDGE,"E14")])]}),"instanceName":"1"});
            var Q3;
            Q3=makeQuery(id+"F16.opPattern","COPY",BODY,{"derivedFrom":makeQuery(id+"F15.opPattern","COPY",BODY,{"derivedFrom":makeQuery(id+"F9.opExtrude","SWEPT_BODY",BODY,{"disambiguationData":[OSD([sQuery(id+"F8.wireOp",EDGE,"E7.0"),sQuery(id+"F8.wireOp",EDGE,"E10"),sQuery(id+"F8.wireOp",EDGE,"E11"),sQuery(id+"F8.wireOp",EDGE,"E12.1.0"),sQuery(id+"F8.wireOp",EDGE,"E12.1.1"),sQuery(id+"F8.wireOp",EDGE,"E12.2.0"),sQuery(id+"F8.wireOp",EDGE,"E12.2.1"),sQuery(id+"F8.wireOp",EDGE,"E12.3.0"),sQuery(id+"F8.wireOp",EDGE,"E12.3.1"),sQuery(id+"F8.wireOp",EDGE,"E12.4.0"),sQuery(id+"F8.wireOp",EDGE,"E12.4.1"),sQuery(id+"F8.wireOp",EDGE,"E12.5.0"),sQuery(id+"F8.wireOp",EDGE,"E12.5.1"),sQuery(id+"F8.wireOp",EDGE,"E12.6.0"),sQuery(id+"F8.wireOp",EDGE,"E13"),sQuery(id+"F8.wireOp",EDGE,"E14")])]}),"instanceName":"1"}),"instanceName":"1"});
            var Q4;
            Q4=sQuery(id+"F25.wireOp",EDGE,"E27");
            circularPattern(context, id + "F26", {"entities" : qUnion([Q0, Q1, Q2, Q3]), "axis" : qUnion([Q4]), "angle" : 72 * degree, "instanceCount" : round(3), "oppositeDirection" : true});
        }
        {
            var Q0;
            Q0=makeQuery(id+"F17.opPattern","COPY",FACE,{"derivedFrom":makeQuery(id+"F3.opExtrude","CAP_FACE",FACE,{"disambiguationData":[OSD([sQuery(id+"F1.wireOp",EDGE,"E2.0"),sQuery(id+"F1.wireOp",EDGE,"E2.1"),sQuery(id+"F1.wireOp",EDGE,"E2.2"),sQuery(id+"F1.wireOp",EDGE,"E2.3"),sQuery(id+"F1.wireOp",EDGE,"E2.4"),sQuery(id+"F1.wireOp",EDGE,"E2.5")])],"isStart":true}),"instanceName":"1"});
            var sketch = newSketch(context, id + "F27", { "sketchPlane" : qUnion([Q0])});
            skLineSegment(sketch, "E28", {"start": v(0, -47.28) * mm, "end": v(0, -21.3) * mm});
            skSolve(sketch);
        }
        {
            var Q0;
            Q0=qCreatedBy(makeId("Right.planeOp"),FACE);
            var sketch = newSketch(context, id + "F28", { "sketchPlane" : qUnion([Q0])});
            skLineSegment(sketch, "E29.0", {"start": v(-35.84, -41.3) * mm, "end": v(-30.97, -15.77) * mm});
            skLineSegment(sketch, "E30", {"start": v(-33.4, -28.53) * mm, "end": v(-47.6, -25.82) * mm});
            skSolve(sketch);
        }
        {
            var Q0;
            Q0=makeQuery(id+"F18.opPattern","COPY",BODY,{"derivedFrom":makeQuery(id+"F2.opExtrude","SWEPT_BODY",BODY,{"disambiguationData":[OSD([sQuery(id+"F0.wireOp",EDGE,"E0.0"),sQuery(id+"F0.wireOp",EDGE,"E0.1"),sQuery(id+"F0.wireOp",EDGE,"E0.2"),sQuery(id+"F0.wireOp",EDGE,"E0.3"),sQuery(id+"F0.wireOp",EDGE,"E0.4")])]}),"instanceName":"2"});
            var Q1;
            Q1=sQuery(id+"F28.wireOp",EDGE,"E30");
            circularPattern(context, id + "F29", {"entities" : qUnion([Q0]), "axis" : qUnion([Q1]), "angle" : 120 * degree, "instanceCount" : 2, "oppositeDirection" : true});
        }
        {
            var Q0;
            Q0=makeQuery(id+"F29.opPattern","COPY",FACE,{"derivedFrom":makeQuery(id+"F18.opPattern","COPY",FACE,{"derivedFrom":makeQuery(id+"F2.opExtrude","CAP_FACE",FACE,{"disambiguationData":[OSD([sQuery(id+"F0.wireOp",EDGE,"E0.0"),sQuery(id+"F0.wireOp",EDGE,"E0.1"),sQuery(id+"F0.wireOp",EDGE,"E0.2"),sQuery(id+"F0.wireOp",EDGE,"E0.3"),sQuery(id+"F0.wireOp",EDGE,"E0.4")])],"isStart":true}),"instanceName":"2"}),"instanceName":"1"});
            var sketch = newSketch(context, id + "F30", { "sketchPlane" : qUnion([Q0])});
            skLineSegment(sketch, "E31", {"start": v(0, -43.99) * mm, "end": v(0, -31.23) * mm});
            skLineSegment(sketch, "E32", {"start": v(-12.14, -35.17) * mm, "end": v(9.82, -28.04) * mm});
            skPoint(sketch, "E33.orphan", {"position": v(0, -20.9) * mm});
            skSolve(sketch);
        }
        {
            var Q0;
            Q0=qCreatedBy(makeId("Right.planeOp"),FACE);
            var sketch = newSketch(context, id + "F31", { "sketchPlane" : qUnion([Q0])});
            skLineSegment(sketch, "E34.0", {"start": v(-25.52, -61.94) * mm, "end": v(-31.23, -50.52) * mm});
            skLineSegment(sketch, "E35", {"start": v(-31.23, -50.52) * mm, "end": v(-51.07, -60.45) * mm});
            skSolve(sketch);
        }
        {
            var Q0;
            Q0=makeQuery(id+"F26.opPattern","COPY",BODY,{"derivedFrom":makeQuery(id+"F3.opExtrude","SWEPT_BODY",BODY,{"disambiguationData":[OSD([sQuery(id+"F1.wireOp",EDGE,"E2.0"),sQuery(id+"F1.wireOp",EDGE,"E2.1"),sQuery(id+"F1.wireOp",EDGE,"E2.2"),sQuery(id+"F1.wireOp",EDGE,"E2.3"),sQuery(id+"F1.wireOp",EDGE,"E2.4"),sQuery(id+"F1.wireOp",EDGE,"E2.5")])]}),"instanceName":"2"});
            var Q1;
            Q1=makeQuery(id+"F26.opPattern","COPY",BODY,{"derivedFrom":makeQuery(id+"F16.opPattern","COPY",BODY,{"derivedFrom":makeQuery(id+"F15.opPattern","COPY",BODY,{"derivedFrom":makeQuery(id+"F9.opExtrude","SWEPT_BODY",BODY,{"disambiguationData":[OSD([sQuery(id+"F8.wireOp",EDGE,"E7.0"),sQuery(id+"F8.wireOp",EDGE,"E10"),sQuery(id+"F8.wireOp",EDGE,"E11"),sQuery(id+"F8.wireOp",EDGE,"E12.1.0"),sQuery(id+"F8.wireOp",EDGE,"E12.1.1"),sQuery(id+"F8.wireOp",EDGE,"E12.2.0"),sQuery(id+"F8.wireOp",EDGE,"E12.2.1"),sQuery(id+"F8.wireOp",EDGE,"E12.3.0"),sQuery(id+"F8.wireOp",EDGE,"E12.3.1"),sQuery(id+"F8.wireOp",EDGE,"E12.4.0"),sQuery(id+"F8.wireOp",EDGE,"E12.4.1"),sQuery(id+"F8.wireOp",EDGE,"E12.5.0"),sQuery(id+"F8.wireOp",EDGE,"E12.5.1"),sQuery(id+"F8.wireOp",EDGE,"E12.6.0"),sQuery(id+"F8.wireOp",EDGE,"E13"),sQuery(id+"F8.wireOp",EDGE,"E14")])]}),"instanceName":"2"}),"instanceName":"1"}),"instanceName":"2"});
            var Q2;
            Q2=makeQuery(id+"F26.opPattern","COPY",BODY,{"derivedFrom":makeQuery(id+"F13.opPattern","COPY",BODY,{"derivedFrom":makeQuery(id+"F9.opExtrude","SWEPT_BODY",BODY,{"disambiguationData":[OSD([sQuery(id+"F8.wireOp",EDGE,"E7.0"),sQuery(id+"F8.wireOp",EDGE,"E10"),sQuery(id+"F8.wireOp",EDGE,"E11"),sQuery(id+"F8.wireOp",EDGE,"E12.1.0"),sQuery(id+"F8.wireOp",EDGE,"E12.1.1"),sQuery(id+"F8.wireOp",EDGE,"E12.2.0"),sQuery(id+"F8.wireOp",EDGE,"E12.2.1"),sQuery(id+"F8.wireOp",EDGE,"E12.3.0"),sQuery(id+"F8.wireOp",EDGE,"E12.3.1"),sQuery(id+"F8.wireOp",EDGE,"E12.4.0"),sQuery(id+"F8.wireOp",EDGE,"E12.4.1"),sQuery(id+"F8.wireOp",EDGE,"E12.5.0"),sQuery(id+"F8.wireOp",EDGE,"E12.5.1"),sQuery(id+"F8.wireOp",EDGE,"E12.6.0"),sQuery(id+"F8.wireOp",EDGE,"E13"),sQuery(id+"F8.wireOp",EDGE,"E14")])]}),"instanceName":"1"}),"instanceName":"2"});
            var Q3;
            Q3=makeQuery(id+"F18.opPattern","COPY",BODY,{"derivedFrom":makeQuery(id+"F13.opPattern","COPY",BODY,{"derivedFrom":makeQuery(id+"F9.opExtrude","SWEPT_BODY",BODY,{"disambiguationData":[OSD([sQuery(id+"F8.wireOp",EDGE,"E7.0"),sQuery(id+"F8.wireOp",EDGE,"E10"),sQuery(id+"F8.wireOp",EDGE,"E11"),sQuery(id+"F8.wireOp",EDGE,"E12.1.0"),sQuery(id+"F8.wireOp",EDGE,"E12.1.1"),sQuery(id+"F8.wireOp",EDGE,"E12.2.0"),sQuery(id+"F8.wireOp",EDGE,"E12.2.1"),sQuery(id+"F8.wireOp",EDGE,"E12.3.0"),sQuery(id+"F8.wireOp",EDGE,"E12.3.1"),sQuery(id+"F8.wireOp",EDGE,"E12.4.0"),sQuery(id+"F8.wireOp",EDGE,"E12.4.1"),sQuery(id+"F8.wireOp",EDGE,"E12.5.0"),sQuery(id+"F8.wireOp",EDGE,"E12.5.1"),sQuery(id+"F8.wireOp",EDGE,"E12.6.0"),sQuery(id+"F8.wireOp",EDGE,"E13"),sQuery(id+"F8.wireOp",EDGE,"E14")])]}),"instanceName":"2"}),"instanceName":"2"});
            var Q4;
            Q4=sQuery(id+"F31.wireOp",EDGE,"E35");
            circularPattern(context, id + "F32", {"entities" : qUnion([Q0, Q1, Q2, Q3]), "axis" : qUnion([Q4]), "angle" : 72 * degree, "instanceCount" : round(3), "oppositeDirection" : true});
        }
        {
            var Q0;
            Q0=makeQuery(id+"F6.opPattern","COPY",FACE,{"derivedFrom":makeQuery(id+"F3.opExtrude","CAP_FACE",FACE,{"disambiguationData":[OSD([sQuery(id+"F1.wireOp",EDGE,"E2.0"),sQuery(id+"F1.wireOp",EDGE,"E2.1"),sQuery(id+"F1.wireOp",EDGE,"E2.2"),sQuery(id+"F1.wireOp",EDGE,"E2.3"),sQuery(id+"F1.wireOp",EDGE,"E2.4"),sQuery(id+"F1.wireOp",EDGE,"E2.5")])],"isStart":true}),"instanceName":"2"});
            var sketch = newSketch(context, id + "F33", { "sketchPlane" : qUnion([Q0])});
            skLineSegment(sketch, "E36", {"start": v(-4.1, 7.1) * mm, "end": v(-17.1, 29.6) * mm});
            skSolve(sketch);
        }
        {
            var Q0;
            Q0=sQuery(id+"F33.wireOp",VERTEX,"E36.end");
            var Q1;
            Q1=sQuery(id+"F33.wireOp",VERTEX,"E36.start");
            var Q2;
            Q2=sQuery(id+"F11.wireOp",VERTEX,"E16.end");
            cPlane(context, id + "F34", {"entities" : qUnion([Q0, Q1, Q2]), "cplaneType" : CPlaneType.THREE_POINT, "offset" : 150 * mm, "width" : 150 * mm, "height" : 150 * mm});
        }
        {
            var Q0;
            Q0=qCreatedBy(id+"F34.planeOp",FACE);
            var sketch = newSketch(context, id + "F35", { "sketchPlane" : qUnion([Q0])});
            skLineSegment(sketch, "E37.0", {"start": v(10.32, 0) * mm, "end": v(30.97, -15.77) * mm});
            skLineSegment(sketch, "E38", {"start": v(20.65, -7.89) * mm, "end": v(38.57, 15.58) * mm});
            skSolve(sketch);
        }
        {
            var Q0;
            Q0=makeQuery(id+"F2.opExtrude","SWEPT_BODY",BODY,{"disambiguationData":[OSD([sQuery(id+"F0.wireOp",EDGE,"E0.0"),sQuery(id+"F0.wireOp",EDGE,"E0.1"),sQuery(id+"F0.wireOp",EDGE,"E0.2"),sQuery(id+"F0.wireOp",EDGE,"E0.3"),sQuery(id+"F0.wireOp",EDGE,"E0.4")])]});
            var Q1;
            Q1=sQuery(id+"F35.wireOp",EDGE,"E38");
            circularPattern(context, id + "F36", {"entities" : qUnion([Q0]), "axis" : qUnion([Q1]), "angle" : 120 * degree, "instanceCount" : round(3), "oppositeDirection" : true});
        }
        {
            var Q0;
            Q0=makeQuery(id+"F36.opPattern","COPY",FACE,{"derivedFrom":makeQuery(id+"F2.opExtrude","CAP_FACE",FACE,{"disambiguationData":[OSD([sQuery(id+"F0.wireOp",EDGE,"E0.0"),sQuery(id+"F0.wireOp",EDGE,"E0.1"),sQuery(id+"F0.wireOp",EDGE,"E0.2"),sQuery(id+"F0.wireOp",EDGE,"E0.3"),sQuery(id+"F0.wireOp",EDGE,"E0.4")])],"isStart":true}),"instanceName":"1"});
            var sketch = newSketch(context, id + "F37", { "sketchPlane" : qUnion([Q0])});
            skLineSegment(sketch, "E39", {"start": v(-4.5, -30.9) * mm, "end": v(1.45, -42.2) * mm});
            skPoint(sketch, "E40.orphan", {"position": v(-9.3, -21.76) * mm});
            skSolve(sketch);
        }
        {
            var Q0;
            Q0=sQuery(id+"F37.wireOp",VERTEX,"E39.end");
            var Q1;
            Q1=sQuery(id+"F37.wireOp",VERTEX,"E39.start");
            var Q2;
            Q2=sQuery(id+"F35.wireOp",VERTEX,"E38.end");
            cPlane(context, id + "F38", {"entities" : qUnion([Q0, Q1, Q2]), "cplaneType" : CPlaneType.THREE_POINT, "offset" : 150 * mm, "width" : 150 * mm, "height" : 150 * mm});
        }
        {
            var Q0;
            Q0=qCreatedBy(id+"F38.planeOp",FACE);
            var sketch = newSketch(context, id + "F39", { "sketchPlane" : qUnion([Q0])});
            skLineSegment(sketch, "E41.0", {"start": v(29.7, -11.34) * mm, "end": v(36.4, -22.2) * mm});
            skLineSegment(sketch, "E42", {"start": v(29.7, -11.34) * mm, "end": v(58.3, 6.33) * mm});
            skSolve(sketch);
        }
        {
            var Q0;
            Q0=makeQuery(id+"F22.opPattern","COPY",BODY,{"derivedFrom":makeQuery(id+"F17.opPattern","COPY",BODY,{"derivedFrom":makeQuery(id+"F3.opExtrude","SWEPT_BODY",BODY,{"disambiguationData":[OSD([sQuery(id+"F1.wireOp",EDGE,"E2.0"),sQuery(id+"F1.wireOp",EDGE,"E2.1"),sQuery(id+"F1.wireOp",EDGE,"E2.2"),sQuery(id+"F1.wireOp",EDGE,"E2.3"),sQuery(id+"F1.wireOp",EDGE,"E2.4"),sQuery(id+"F1.wireOp",EDGE,"E2.5")])]}),"instanceName":"1"}),"instanceName":"2"});
            var Q1;
            Q1=makeQuery(id+"F22.opPattern","COPY",BODY,{"derivedFrom":makeQuery(id+"F17.opPattern","COPY",BODY,{"derivedFrom":makeQuery(id+"F16.opPattern","COPY",BODY,{"derivedFrom":makeQuery(id+"F15.opPattern","COPY",BODY,{"derivedFrom":makeQuery(id+"F9.opExtrude","SWEPT_BODY",BODY,{"disambiguationData":[OSD([sQuery(id+"F8.wireOp",EDGE,"E7.0"),sQuery(id+"F8.wireOp",EDGE,"E10"),sQuery(id+"F8.wireOp",EDGE,"E11"),sQuery(id+"F8.wireOp",EDGE,"E12.1.0"),sQuery(id+"F8.wireOp",EDGE,"E12.1.1"),sQuery(id+"F8.wireOp",EDGE,"E12.2.0"),sQuery(id+"F8.wireOp",EDGE,"E12.2.1"),sQuery(id+"F8.wireOp",EDGE,"E12.3.0"),sQuery(id+"F8.wireOp",EDGE,"E12.3.1"),sQuery(id+"F8.wireOp",EDGE,"E12.4.0"),sQuery(id+"F8.wireOp",EDGE,"E12.4.1"),sQuery(id+"F8.wireOp",EDGE,"E12.5.0"),sQuery(id+"F8.wireOp",EDGE,"E12.5.1"),sQuery(id+"F8.wireOp",EDGE,"E12.6.0"),sQuery(id+"F8.wireOp",EDGE,"E13"),sQuery(id+"F8.wireOp",EDGE,"E14")])]}),"instanceName":"2"}),"instanceName":"1"}),"instanceName":"1"}),"instanceName":"2"});
            var Q2;
            Q2=makeQuery(id+"F22.opPattern","COPY",BODY,{"derivedFrom":makeQuery(id+"F17.opPattern","COPY",BODY,{"derivedFrom":makeQuery(id+"F13.opPattern","COPY",BODY,{"derivedFrom":makeQuery(id+"F9.opExtrude","SWEPT_BODY",BODY,{"disambiguationData":[OSD([sQuery(id+"F8.wireOp",EDGE,"E7.0"),sQuery(id+"F8.wireOp",EDGE,"E10"),sQuery(id+"F8.wireOp",EDGE,"E11"),sQuery(id+"F8.wireOp",EDGE,"E12.1.0"),sQuery(id+"F8.wireOp",EDGE,"E12.1.1"),sQuery(id+"F8.wireOp",EDGE,"E12.2.0"),sQuery(id+"F8.wireOp",EDGE,"E12.2.1"),sQuery(id+"F8.wireOp",EDGE,"E12.3.0"),sQuery(id+"F8.wireOp",EDGE,"E12.3.1"),sQuery(id+"F8.wireOp",EDGE,"E12.4.0"),sQuery(id+"F8.wireOp",EDGE,"E12.4.1"),sQuery(id+"F8.wireOp",EDGE,"E12.5.0"),sQuery(id+"F8.wireOp",EDGE,"E12.5.1"),sQuery(id+"F8.wireOp",EDGE,"E12.6.0"),sQuery(id+"F8.wireOp",EDGE,"E13"),sQuery(id+"F8.wireOp",EDGE,"E14")])]}),"instanceName":"1"}),"instanceName":"1"}),"instanceName":"2"});
            var Q3;
            Q3=makeQuery(id+"F18.opPattern","COPY",BODY,{"derivedFrom":makeQuery(id+"F13.opPattern","COPY",BODY,{"derivedFrom":makeQuery(id+"F9.opExtrude","SWEPT_BODY",BODY,{"disambiguationData":[OSD([sQuery(id+"F8.wireOp",EDGE,"E7.0"),sQuery(id+"F8.wireOp",EDGE,"E10"),sQuery(id+"F8.wireOp",EDGE,"E11"),sQuery(id+"F8.wireOp",EDGE,"E12.1.0"),sQuery(id+"F8.wireOp",EDGE,"E12.1.1"),sQuery(id+"F8.wireOp",EDGE,"E12.2.0"),sQuery(id+"F8.wireOp",EDGE,"E12.2.1"),sQuery(id+"F8.wireOp",EDGE,"E12.3.0"),sQuery(id+"F8.wireOp",EDGE,"E12.3.1"),sQuery(id+"F8.wireOp",EDGE,"E12.4.0"),sQuery(id+"F8.wireOp",EDGE,"E12.4.1"),sQuery(id+"F8.wireOp",EDGE,"E12.5.0"),sQuery(id+"F8.wireOp",EDGE,"E12.5.1"),sQuery(id+"F8.wireOp",EDGE,"E12.6.0"),sQuery(id+"F8.wireOp",EDGE,"E13"),sQuery(id+"F8.wireOp",EDGE,"E14")])]}),"instanceName":"2"}),"instanceName":"1"});
            var Q4;
            Q4=sQuery(id+"F39.wireOp",EDGE,"E42");
            circularPattern(context, id + "F40", {"entities" : qUnion([Q0, Q1, Q2, Q3]), "axis" : qUnion([Q4]), "angle" : 72 * degree, "instanceCount" : round(3), "oppositeDirection" : true});
        }
        {
            var Q0;
            Q0=makeQuery(id+"F36.opPattern","COPY",FACE,{"derivedFrom":makeQuery(id+"F2.opExtrude","CAP_FACE",FACE,{"disambiguationData":[OSD([sQuery(id+"F0.wireOp",EDGE,"E0.0"),sQuery(id+"F0.wireOp",EDGE,"E0.1"),sQuery(id+"F0.wireOp",EDGE,"E0.2"),sQuery(id+"F0.wireOp",EDGE,"E0.3"),sQuery(id+"F0.wireOp",EDGE,"E0.4")])],"isStart":true}),"instanceName":"2"});
            var sketch = newSketch(context, id + "F41", { "sketchPlane" : qUnion([Q0])});
            skLineSegment(sketch, "E43", {"start": v(0, -18.47) * mm, "end": v(0, -31.23) * mm});
            skPoint(sketch, "E44.orphan", {"position": v(0, -41.55) * mm});
            skSolve(sketch);
        }
        {
            var Q0;
            Q0=sQuery(id+"F41.wireOp",VERTEX,"E43.end");
            var Q1;
            Q1=sQuery(id+"F41.wireOp",VERTEX,"E43.start");
            var Q2;
            Q2=sQuery(id+"F11.wireOp",VERTEX,"E16.end");
            cPlane(context, id + "F42", {"entities" : qUnion([Q0, Q1, Q2]), "cplaneType" : CPlaneType.THREE_POINT, "offset" : 150 * mm, "width" : 150 * mm, "height" : 150 * mm});
        }
        {
            var Q0;
            Q0=qCreatedBy(id+"F42.planeOp",FACE);
            var sketch = newSketch(context, id + "F43", { "sketchPlane" : qUnion([Q0])});
            skLineSegment(sketch, "E45.0", {"start": v(-25.52, -7.89) * mm, "end": v(-31.23, -19.3) * mm});
            skLineSegment(sketch, "E46", {"start": v(-31.23, -19.3) * mm, "end": v(-78.41, 4.3) * mm});
            skSolve(sketch);
        }
        {
            var Q0;
            Q0=makeQuery(id+"F40.opPattern","COPY",BODY,{"derivedFrom":makeQuery(id+"F22.opPattern","COPY",BODY,{"derivedFrom":makeQuery(id+"F17.opPattern","COPY",BODY,{"derivedFrom":makeQuery(id+"F3.opExtrude","SWEPT_BODY",BODY,{"disambiguationData":[OSD([sQuery(id+"F1.wireOp",EDGE,"E2.0"),sQuery(id+"F1.wireOp",EDGE,"E2.1"),sQuery(id+"F1.wireOp",EDGE,"E2.2"),sQuery(id+"F1.wireOp",EDGE,"E2.3"),sQuery(id+"F1.wireOp",EDGE,"E2.4"),sQuery(id+"F1.wireOp",EDGE,"E2.5")])]}),"instanceName":"1"}),"instanceName":"2"}),"instanceName":"2"});
            var Q1;
            Q1=makeQuery(id+"F40.opPattern","COPY",BODY,{"derivedFrom":makeQuery(id+"F22.opPattern","COPY",BODY,{"derivedFrom":makeQuery(id+"F17.opPattern","COPY",BODY,{"derivedFrom":makeQuery(id+"F13.opPattern","COPY",BODY,{"derivedFrom":makeQuery(id+"F9.opExtrude","SWEPT_BODY",BODY,{"disambiguationData":[OSD([sQuery(id+"F8.wireOp",EDGE,"E7.0"),sQuery(id+"F8.wireOp",EDGE,"E10"),sQuery(id+"F8.wireOp",EDGE,"E11"),sQuery(id+"F8.wireOp",EDGE,"E12.1.0"),sQuery(id+"F8.wireOp",EDGE,"E12.1.1"),sQuery(id+"F8.wireOp",EDGE,"E12.2.0"),sQuery(id+"F8.wireOp",EDGE,"E12.2.1"),sQuery(id+"F8.wireOp",EDGE,"E12.3.0"),sQuery(id+"F8.wireOp",EDGE,"E12.3.1"),sQuery(id+"F8.wireOp",EDGE,"E12.4.0"),sQuery(id+"F8.wireOp",EDGE,"E12.4.1"),sQuery(id+"F8.wireOp",EDGE,"E12.5.0"),sQuery(id+"F8.wireOp",EDGE,"E12.5.1"),sQuery(id+"F8.wireOp",EDGE,"E12.6.0"),sQuery(id+"F8.wireOp",EDGE,"E13"),sQuery(id+"F8.wireOp",EDGE,"E14")])]}),"instanceName":"1"}),"instanceName":"1"}),"instanceName":"2"}),"instanceName":"2"});
            var Q2;
            Q2=makeQuery(id+"F40.opPattern","COPY",BODY,{"derivedFrom":makeQuery(id+"F18.opPattern","COPY",BODY,{"derivedFrom":makeQuery(id+"F13.opPattern","COPY",BODY,{"derivedFrom":makeQuery(id+"F9.opExtrude","SWEPT_BODY",BODY,{"disambiguationData":[OSD([sQuery(id+"F8.wireOp",EDGE,"E7.0"),sQuery(id+"F8.wireOp",EDGE,"E10"),sQuery(id+"F8.wireOp",EDGE,"E11"),sQuery(id+"F8.wireOp",EDGE,"E12.1.0"),sQuery(id+"F8.wireOp",EDGE,"E12.1.1"),sQuery(id+"F8.wireOp",EDGE,"E12.2.0"),sQuery(id+"F8.wireOp",EDGE,"E12.2.1"),sQuery(id+"F8.wireOp",EDGE,"E12.3.0"),sQuery(id+"F8.wireOp",EDGE,"E12.3.1"),sQuery(id+"F8.wireOp",EDGE,"E12.4.0"),sQuery(id+"F8.wireOp",EDGE,"E12.4.1"),sQuery(id+"F8.wireOp",EDGE,"E12.5.0"),sQuery(id+"F8.wireOp",EDGE,"E12.5.1"),sQuery(id+"F8.wireOp",EDGE,"E12.6.0"),sQuery(id+"F8.wireOp",EDGE,"E13"),sQuery(id+"F8.wireOp",EDGE,"E14")])]}),"instanceName":"2"}),"instanceName":"1"}),"instanceName":"2"});
            var Q3;
            Q3=makeQuery(id+"F40.opPattern","COPY",BODY,{"derivedFrom":makeQuery(id+"F22.opPattern","COPY",BODY,{"derivedFrom":makeQuery(id+"F17.opPattern","COPY",BODY,{"derivedFrom":makeQuery(id+"F16.opPattern","COPY",BODY,{"derivedFrom":makeQuery(id+"F15.opPattern","COPY",BODY,{"derivedFrom":makeQuery(id+"F9.opExtrude","SWEPT_BODY",BODY,{"disambiguationData":[OSD([sQuery(id+"F8.wireOp",EDGE,"E7.0"),sQuery(id+"F8.wireOp",EDGE,"E10"),sQuery(id+"F8.wireOp",EDGE,"E11"),sQuery(id+"F8.wireOp",EDGE,"E12.1.0"),sQuery(id+"F8.wireOp",EDGE,"E12.1.1"),sQuery(id+"F8.wireOp",EDGE,"E12.2.0"),sQuery(id+"F8.wireOp",EDGE,"E12.2.1"),sQuery(id+"F8.wireOp",EDGE,"E12.3.0"),sQuery(id+"F8.wireOp",EDGE,"E12.3.1"),sQuery(id+"F8.wireOp",EDGE,"E12.4.0"),sQuery(id+"F8.wireOp",EDGE,"E12.4.1"),sQuery(id+"F8.wireOp",EDGE,"E12.5.0"),sQuery(id+"F8.wireOp",EDGE,"E12.5.1"),sQuery(id+"F8.wireOp",EDGE,"E12.6.0"),sQuery(id+"F8.wireOp",EDGE,"E13"),sQuery(id+"F8.wireOp",EDGE,"E14")])]}),"instanceName":"2"}),"instanceName":"1"}),"instanceName":"1"}),"instanceName":"2"}),"instanceName":"2"});
            var Q4;
            Q4=sQuery(id+"F43.wireOp",EDGE,"E46");
            circularPattern(context, id + "F44", {"entities" : qUnion([Q0, Q1, Q2, Q3]), "axis" : qUnion([Q4]), "angle" : 72 * degree, "instanceCount" : round(3), "oppositeDirection" : true});
        }
        {
            var Q0;
            Q0=makeQuery(id+"F40.opPattern","COPY",FACE,{"derivedFrom":makeQuery(id+"F22.opPattern","COPY",FACE,{"derivedFrom":makeQuery(id+"F17.opPattern","COPY",FACE,{"derivedFrom":makeQuery(id+"F3.opExtrude","CAP_FACE",FACE,{"disambiguationData":[OSD([sQuery(id+"F1.wireOp",EDGE,"E2.0"),sQuery(id+"F1.wireOp",EDGE,"E2.1"),sQuery(id+"F1.wireOp",EDGE,"E2.2"),sQuery(id+"F1.wireOp",EDGE,"E2.3"),sQuery(id+"F1.wireOp",EDGE,"E2.4"),sQuery(id+"F1.wireOp",EDGE,"E2.5")])],"isStart":true}),"instanceName":"1"}),"instanceName":"2"}),"instanceName":"1"});
            var sketch = newSketch(context, id + "F45", { "sketchPlane" : qUnion([Q0])});
            skLineSegment(sketch, "E47", {"start": v(1.3, -21.26) * mm, "end": v(2.09, -34.23) * mm});
            skSolve(sketch);
        }
        {
            var Q0;
            Q0=sQuery(id+"F45.wireOp",VERTEX,"E47.end");
            var Q1;
            Q1=sQuery(id+"F45.wireOp",VERTEX,"E47.start");
            var Q2;
            Q2=makeQuery(id+"F6.opPattern","COPY",VERTEX,{"derivedFrom":makeQuery(id+"F3.opExtrude","CAP_VERTEX",VERTEX,{"disambiguationData":[OSD([sQuery(id+"F1.wireOp",EDGE,"E2.1"),sQuery(id+"F1.wireOp",EDGE,"E2.2")])],"isStart":true}),"instanceName":"3"});
            cPlane(context, id + "F46", {"entities" : qUnion([Q0, Q1, Q2]), "cplaneType" : CPlaneType.THREE_POINT, "offset" : 150 * mm, "width" : 150 * mm, "height" : 150 * mm});
        }
        {
            var Q0;
            Q0=qCreatedBy(id+"F46.planeOp",FACE);
            var sketch = newSketch(context, id + "F47", { "sketchPlane" : qUnion([Q0])});
            skLineSegment(sketch, "E48.0", {"start": v(-35.84, -28.53) * mm, "end": v(-33.4, -41.3) * mm});
            skLineSegment(sketch, "E49", {"start": v(-33.4, -41.3) * mm, "end": v(-61.9, -46.73) * mm});
            skSolve(sketch);
        }
        {
            var Q0;
            Q0=makeQuery(id+"F22.opPattern","COPY",BODY,{"derivedFrom":makeQuery(id+"F17.opPattern","COPY",BODY,{"derivedFrom":makeQuery(id+"F3.opExtrude","SWEPT_BODY",BODY,{"disambiguationData":[OSD([sQuery(id+"F1.wireOp",EDGE,"E2.0"),sQuery(id+"F1.wireOp",EDGE,"E2.1"),sQuery(id+"F1.wireOp",EDGE,"E2.2"),sQuery(id+"F1.wireOp",EDGE,"E2.3"),sQuery(id+"F1.wireOp",EDGE,"E2.4"),sQuery(id+"F1.wireOp",EDGE,"E2.5")])]}),"instanceName":"1"}),"instanceName":"2"});
            var Q1;
            Q1=makeQuery(id+"F22.opPattern","COPY",BODY,{"derivedFrom":makeQuery(id+"F17.opPattern","COPY",BODY,{"derivedFrom":makeQuery(id+"F13.opPattern","COPY",BODY,{"derivedFrom":makeQuery(id+"F9.opExtrude","SWEPT_BODY",BODY,{"disambiguationData":[OSD([sQuery(id+"F8.wireOp",EDGE,"E7.0"),sQuery(id+"F8.wireOp",EDGE,"E10"),sQuery(id+"F8.wireOp",EDGE,"E11"),sQuery(id+"F8.wireOp",EDGE,"E12.1.0"),sQuery(id+"F8.wireOp",EDGE,"E12.1.1"),sQuery(id+"F8.wireOp",EDGE,"E12.2.0"),sQuery(id+"F8.wireOp",EDGE,"E12.2.1"),sQuery(id+"F8.wireOp",EDGE,"E12.3.0"),sQuery(id+"F8.wireOp",EDGE,"E12.3.1"),sQuery(id+"F8.wireOp",EDGE,"E12.4.0"),sQuery(id+"F8.wireOp",EDGE,"E12.4.1"),sQuery(id+"F8.wireOp",EDGE,"E12.5.0"),sQuery(id+"F8.wireOp",EDGE,"E12.5.1"),sQuery(id+"F8.wireOp",EDGE,"E12.6.0"),sQuery(id+"F8.wireOp",EDGE,"E13"),sQuery(id+"F8.wireOp",EDGE,"E14")])]}),"instanceName":"1"}),"instanceName":"1"}),"instanceName":"2"});
            var Q2;
            Q2=makeQuery(id+"F22.opPattern","COPY",BODY,{"derivedFrom":makeQuery(id+"F17.opPattern","COPY",BODY,{"derivedFrom":makeQuery(id+"F16.opPattern","COPY",BODY,{"derivedFrom":makeQuery(id+"F15.opPattern","COPY",BODY,{"derivedFrom":makeQuery(id+"F9.opExtrude","SWEPT_BODY",BODY,{"disambiguationData":[OSD([sQuery(id+"F8.wireOp",EDGE,"E7.0"),sQuery(id+"F8.wireOp",EDGE,"E10"),sQuery(id+"F8.wireOp",EDGE,"E11"),sQuery(id+"F8.wireOp",EDGE,"E12.1.0"),sQuery(id+"F8.wireOp",EDGE,"E12.1.1"),sQuery(id+"F8.wireOp",EDGE,"E12.2.0"),sQuery(id+"F8.wireOp",EDGE,"E12.2.1"),sQuery(id+"F8.wireOp",EDGE,"E12.3.0"),sQuery(id+"F8.wireOp",EDGE,"E12.3.1"),sQuery(id+"F8.wireOp",EDGE,"E12.4.0"),sQuery(id+"F8.wireOp",EDGE,"E12.4.1"),sQuery(id+"F8.wireOp",EDGE,"E12.5.0"),sQuery(id+"F8.wireOp",EDGE,"E12.5.1"),sQuery(id+"F8.wireOp",EDGE,"E12.6.0"),sQuery(id+"F8.wireOp",EDGE,"E13"),sQuery(id+"F8.wireOp",EDGE,"E14")])]}),"instanceName":"2"}),"instanceName":"1"}),"instanceName":"1"}),"instanceName":"2"});
            var Q3;
            Q3=makeQuery(id+"F18.opPattern","COPY",BODY,{"derivedFrom":makeQuery(id+"F13.opPattern","COPY",BODY,{"derivedFrom":makeQuery(id+"F9.opExtrude","SWEPT_BODY",BODY,{"disambiguationData":[OSD([sQuery(id+"F8.wireOp",EDGE,"E7.0"),sQuery(id+"F8.wireOp",EDGE,"E10"),sQuery(id+"F8.wireOp",EDGE,"E11"),sQuery(id+"F8.wireOp",EDGE,"E12.1.0"),sQuery(id+"F8.wireOp",EDGE,"E12.1.1"),sQuery(id+"F8.wireOp",EDGE,"E12.2.0"),sQuery(id+"F8.wireOp",EDGE,"E12.2.1"),sQuery(id+"F8.wireOp",EDGE,"E12.3.0"),sQuery(id+"F8.wireOp",EDGE,"E12.3.1"),sQuery(id+"F8.wireOp",EDGE,"E12.4.0"),sQuery(id+"F8.wireOp",EDGE,"E12.4.1"),sQuery(id+"F8.wireOp",EDGE,"E12.5.0"),sQuery(id+"F8.wireOp",EDGE,"E12.5.1"),sQuery(id+"F8.wireOp",EDGE,"E12.6.0"),sQuery(id+"F8.wireOp",EDGE,"E13"),sQuery(id+"F8.wireOp",EDGE,"E14")])]}),"instanceName":"2"}),"instanceName":"1"});
            var Q4;
            Q4=sQuery(id+"F47.wireOp",EDGE,"E49");
            circularPattern(context, id + "F48", {"entities" : qUnion([Q0, Q1, Q2, Q3]), "axis" : qUnion([Q4]), "angle" : 120 * degree, "instanceCount" : 2, "oppositeDirection" : true});
        }
        {
            var Q0;
            Q0=makeQuery(id+"F26.opPattern","COPY",FACE,{"derivedFrom":makeQuery(id+"F3.opExtrude","CAP_FACE",FACE,{"disambiguationData":[OSD([sQuery(id+"F1.wireOp",EDGE,"E2.0"),sQuery(id+"F1.wireOp",EDGE,"E2.1"),sQuery(id+"F1.wireOp",EDGE,"E2.2"),sQuery(id+"F1.wireOp",EDGE,"E2.3"),sQuery(id+"F1.wireOp",EDGE,"E2.4"),sQuery(id+"F1.wireOp",EDGE,"E2.5")])],"isStart":true}),"instanceName":"1"});
            var sketch = newSketch(context, id + "F49", { "sketchPlane" : qUnion([Q0])});
            skLineSegment(sketch, "E50", {"start": v(-12.92, -27.06) * mm, "end": v(-2.09, -34.23) * mm});
            skSolve(sketch);
        }
        {
            var Q0;
            Q0=sQuery(id+"F49.wireOp",VERTEX,"E50.end");
            var Q1;
            Q1=sQuery(id+"F49.wireOp",VERTEX,"E50.start");
            var Q2;
            Q2=makeQuery(id+"F6.opPattern","COPY",VERTEX,{"derivedFrom":makeQuery(id+"F3.opExtrude","CAP_VERTEX",VERTEX,{"disambiguationData":[OSD([sQuery(id+"F1.wireOp",EDGE,"E2.0"),sQuery(id+"F1.wireOp",EDGE,"E2.5")])],"isStart":true}),"instanceName":"4"});
            cPlane(context, id + "F50", {"entities" : qUnion([Q0, Q1, Q2]), "cplaneType" : CPlaneType.THREE_POINT, "offset" : 150 * mm, "width" : 150 * mm, "height" : 150 * mm});
        }
        {
            var Q0;
            Q0=qCreatedBy(id+"F50.planeOp",FACE);
            var sketch = newSketch(context, id + "F51", { "sketchPlane" : qUnion([Q0])});
            skLineSegment(sketch, "E51.0", {"start": v(27.14, -5.92) * mm, "end": v(31.77, 6.22) * mm});
            skLineSegment(sketch, "E52", {"start": v(31.77, 6.22) * mm, "end": v(70.56, -8.6) * mm});
            skSolve(sketch);
        }
        {
            var Q0;
            Q0=makeQuery(id+"F16.opPattern","COPY",BODY,{"derivedFrom":makeQuery(id+"F15.opPattern","COPY",BODY,{"derivedFrom":makeQuery(id+"F9.opExtrude","SWEPT_BODY",BODY,{"disambiguationData":[OSD([sQuery(id+"F8.wireOp",EDGE,"E7.0"),sQuery(id+"F8.wireOp",EDGE,"E10"),sQuery(id+"F8.wireOp",EDGE,"E11"),sQuery(id+"F8.wireOp",EDGE,"E12.1.0"),sQuery(id+"F8.wireOp",EDGE,"E12.1.1"),sQuery(id+"F8.wireOp",EDGE,"E12.2.0"),sQuery(id+"F8.wireOp",EDGE,"E12.2.1"),sQuery(id+"F8.wireOp",EDGE,"E12.3.0"),sQuery(id+"F8.wireOp",EDGE,"E12.3.1"),sQuery(id+"F8.wireOp",EDGE,"E12.4.0"),sQuery(id+"F8.wireOp",EDGE,"E12.4.1"),sQuery(id+"F8.wireOp",EDGE,"E12.5.0"),sQuery(id+"F8.wireOp",EDGE,"E12.5.1"),sQuery(id+"F8.wireOp",EDGE,"E12.6.0"),sQuery(id+"F8.wireOp",EDGE,"E13"),sQuery(id+"F8.wireOp",EDGE,"E14")])]}),"instanceName":"1"}),"instanceName":"1"});
            var Q1;
            Q1=makeQuery(id+"F13.opPattern","COPY",BODY,{"derivedFrom":makeQuery(id+"F9.opExtrude","SWEPT_BODY",BODY,{"disambiguationData":[OSD([sQuery(id+"F8.wireOp",EDGE,"E7.0"),sQuery(id+"F8.wireOp",EDGE,"E10"),sQuery(id+"F8.wireOp",EDGE,"E11"),sQuery(id+"F8.wireOp",EDGE,"E12.1.0"),sQuery(id+"F8.wireOp",EDGE,"E12.1.1"),sQuery(id+"F8.wireOp",EDGE,"E12.2.0"),sQuery(id+"F8.wireOp",EDGE,"E12.2.1"),sQuery(id+"F8.wireOp",EDGE,"E12.3.0"),sQuery(id+"F8.wireOp",EDGE,"E12.3.1"),sQuery(id+"F8.wireOp",EDGE,"E12.4.0"),sQuery(id+"F8.wireOp",EDGE,"E12.4.1"),sQuery(id+"F8.wireOp",EDGE,"E12.5.0"),sQuery(id+"F8.wireOp",EDGE,"E12.5.1"),sQuery(id+"F8.wireOp",EDGE,"E12.6.0"),sQuery(id+"F8.wireOp",EDGE,"E13"),sQuery(id+"F8.wireOp",EDGE,"E14")])]}),"instanceName":"1"});
            var Q2;
            Q2=makeQuery(id+"F16.opPattern","COPY",BODY,{"derivedFrom":makeQuery(id+"F15.opPattern","COPY",BODY,{"derivedFrom":makeQuery(id+"F9.opExtrude","SWEPT_BODY",BODY,{"disambiguationData":[OSD([sQuery(id+"F8.wireOp",EDGE,"E7.0"),sQuery(id+"F8.wireOp",EDGE,"E10"),sQuery(id+"F8.wireOp",EDGE,"E11"),sQuery(id+"F8.wireOp",EDGE,"E12.1.0"),sQuery(id+"F8.wireOp",EDGE,"E12.1.1"),sQuery(id+"F8.wireOp",EDGE,"E12.2.0"),sQuery(id+"F8.wireOp",EDGE,"E12.2.1"),sQuery(id+"F8.wireOp",EDGE,"E12.3.0"),sQuery(id+"F8.wireOp",EDGE,"E12.3.1"),sQuery(id+"F8.wireOp",EDGE,"E12.4.0"),sQuery(id+"F8.wireOp",EDGE,"E12.4.1"),sQuery(id+"F8.wireOp",EDGE,"E12.5.0"),sQuery(id+"F8.wireOp",EDGE,"E12.5.1"),sQuery(id+"F8.wireOp",EDGE,"E12.6.0"),sQuery(id+"F8.wireOp",EDGE,"E13"),sQuery(id+"F8.wireOp",EDGE,"E14")])]}),"instanceName":"2"}),"instanceName":"1"});
            var Q3;
            Q3=makeQuery(id+"F3.opExtrude","SWEPT_BODY",BODY,{"disambiguationData":[OSD([sQuery(id+"F1.wireOp",EDGE,"E2.0"),sQuery(id+"F1.wireOp",EDGE,"E2.1"),sQuery(id+"F1.wireOp",EDGE,"E2.2"),sQuery(id+"F1.wireOp",EDGE,"E2.3"),sQuery(id+"F1.wireOp",EDGE,"E2.4"),sQuery(id+"F1.wireOp",EDGE,"E2.5")])]});
            var Q4;
            Q4=sQuery(id+"F51.wireOp",EDGE,"E52");
            circularPattern(context, id + "F52", {"entities" : qUnion([Q0, Q1, Q2, Q3]), "axis" : qUnion([Q4]), "angle" : 120 * degree, "instanceCount" : round(2), "oppositeDirection" : true});
        }
        {
            var Q0;
            Q0=makeQuery(id+"F32.opPattern","COPY",FACE,{"derivedFrom":makeQuery(id+"F26.opPattern","COPY",FACE,{"derivedFrom":makeQuery(id+"F3.opExtrude","CAP_FACE",FACE,{"disambiguationData":[OSD([sQuery(id+"F1.wireOp",EDGE,"E2.0"),sQuery(id+"F1.wireOp",EDGE,"E2.1"),sQuery(id+"F1.wireOp",EDGE,"E2.2"),sQuery(id+"F1.wireOp",EDGE,"E2.3"),sQuery(id+"F1.wireOp",EDGE,"E2.4"),sQuery(id+"F1.wireOp",EDGE,"E2.5")])],"isStart":true}),"instanceName":"2"}),"instanceName":"1"});
            var sketch = newSketch(context, id + "F53", { "sketchPlane" : qUnion([Q0])});
            skLineSegment(sketch, "E53", {"start": v(-10.6, -33.35) * mm, "end": v(-10.6, -18.35) * mm});
            skSolve(sketch);
        }
        {
            var Q0;
            Q0=sQuery(id+"F53.wireOp",VERTEX,"E53.start");
            var Q1;
            Q1=sQuery(id+"F53.wireOp",VERTEX,"E53.end");
            var Q2;
            Q2=makeQuery(id+"F32.opPattern","COPY",VERTEX,{"derivedFrom":makeQuery(id+"F26.opPattern","COPY",VERTEX,{"derivedFrom":makeQuery(id+"F3.opExtrude","CAP_VERTEX",VERTEX,{"disambiguationData":[OSD([sQuery(id+"F1.wireOp",EDGE,"E2.2"),sQuery(id+"F1.wireOp",EDGE,"E2.3")])],"isStart":false}),"instanceName":"2"}),"instanceName":"1"});
            cPlane(context, id + "F54", {"entities" : qUnion([Q0, Q1, Q2]), "cplaneType" : CPlaneType.THREE_POINT, "offset" : 150 * mm, "width" : 150 * mm, "height" : 150 * mm});
        }
        {
            var Q0;
            Q0=qCreatedBy(id+"F54.planeOp",FACE);
            var sketch = newSketch(context, id + "F55", { "sketchPlane" : qUnion([Q0])});
            skLineSegment(sketch, "E54.0", {"start": v(-2, -70.16) * mm, "end": v(-14.98, -62.66) * mm});
            skLineSegment(sketch, "E55", {"start": v(-14.98, -62.66) * mm, "end": v(-37.7, -102) * mm});
            skSolve(sketch);
        }
        {
            var Q0;
            Q0=makeQuery(id+"F26.opPattern","COPY",BODY,{"derivedFrom":makeQuery(id+"F3.opExtrude","SWEPT_BODY",BODY,{"disambiguationData":[OSD([sQuery(id+"F1.wireOp",EDGE,"E2.0"),sQuery(id+"F1.wireOp",EDGE,"E2.1"),sQuery(id+"F1.wireOp",EDGE,"E2.2"),sQuery(id+"F1.wireOp",EDGE,"E2.3"),sQuery(id+"F1.wireOp",EDGE,"E2.4"),sQuery(id+"F1.wireOp",EDGE,"E2.5")])]}),"instanceName":"2"});
            var Q1;
            Q1=makeQuery(id+"F26.opPattern","COPY",BODY,{"derivedFrom":makeQuery(id+"F16.opPattern","COPY",BODY,{"derivedFrom":makeQuery(id+"F15.opPattern","COPY",BODY,{"derivedFrom":makeQuery(id+"F9.opExtrude","SWEPT_BODY",BODY,{"disambiguationData":[OSD([sQuery(id+"F8.wireOp",EDGE,"E7.0"),sQuery(id+"F8.wireOp",EDGE,"E10"),sQuery(id+"F8.wireOp",EDGE,"E11"),sQuery(id+"F8.wireOp",EDGE,"E12.1.0"),sQuery(id+"F8.wireOp",EDGE,"E12.1.1"),sQuery(id+"F8.wireOp",EDGE,"E12.2.0"),sQuery(id+"F8.wireOp",EDGE,"E12.2.1"),sQuery(id+"F8.wireOp",EDGE,"E12.3.0"),sQuery(id+"F8.wireOp",EDGE,"E12.3.1"),sQuery(id+"F8.wireOp",EDGE,"E12.4.0"),sQuery(id+"F8.wireOp",EDGE,"E12.4.1"),sQuery(id+"F8.wireOp",EDGE,"E12.5.0"),sQuery(id+"F8.wireOp",EDGE,"E12.5.1"),sQuery(id+"F8.wireOp",EDGE,"E12.6.0"),sQuery(id+"F8.wireOp",EDGE,"E13"),sQuery(id+"F8.wireOp",EDGE,"E14")])]}),"instanceName":"2"}),"instanceName":"1"}),"instanceName":"2"});
            var Q2;
            Q2=makeQuery(id+"F26.opPattern","COPY",BODY,{"derivedFrom":makeQuery(id+"F13.opPattern","COPY",BODY,{"derivedFrom":makeQuery(id+"F9.opExtrude","SWEPT_BODY",BODY,{"disambiguationData":[OSD([sQuery(id+"F8.wireOp",EDGE,"E7.0"),sQuery(id+"F8.wireOp",EDGE,"E10"),sQuery(id+"F8.wireOp",EDGE,"E11"),sQuery(id+"F8.wireOp",EDGE,"E12.1.0"),sQuery(id+"F8.wireOp",EDGE,"E12.1.1"),sQuery(id+"F8.wireOp",EDGE,"E12.2.0"),sQuery(id+"F8.wireOp",EDGE,"E12.2.1"),sQuery(id+"F8.wireOp",EDGE,"E12.3.0"),sQuery(id+"F8.wireOp",EDGE,"E12.3.1"),sQuery(id+"F8.wireOp",EDGE,"E12.4.0"),sQuery(id+"F8.wireOp",EDGE,"E12.4.1"),sQuery(id+"F8.wireOp",EDGE,"E12.5.0"),sQuery(id+"F8.wireOp",EDGE,"E12.5.1"),sQuery(id+"F8.wireOp",EDGE,"E12.6.0"),sQuery(id+"F8.wireOp",EDGE,"E13"),sQuery(id+"F8.wireOp",EDGE,"E14")])]}),"instanceName":"1"}),"instanceName":"2"});
            var Q3;
            Q3=makeQuery(id+"F18.opPattern","COPY",BODY,{"derivedFrom":makeQuery(id+"F13.opPattern","COPY",BODY,{"derivedFrom":makeQuery(id+"F9.opExtrude","SWEPT_BODY",BODY,{"disambiguationData":[OSD([sQuery(id+"F8.wireOp",EDGE,"E7.0"),sQuery(id+"F8.wireOp",EDGE,"E10"),sQuery(id+"F8.wireOp",EDGE,"E11"),sQuery(id+"F8.wireOp",EDGE,"E12.1.0"),sQuery(id+"F8.wireOp",EDGE,"E12.1.1"),sQuery(id+"F8.wireOp",EDGE,"E12.2.0"),sQuery(id+"F8.wireOp",EDGE,"E12.2.1"),sQuery(id+"F8.wireOp",EDGE,"E12.3.0"),sQuery(id+"F8.wireOp",EDGE,"E12.3.1"),sQuery(id+"F8.wireOp",EDGE,"E12.4.0"),sQuery(id+"F8.wireOp",EDGE,"E12.4.1"),sQuery(id+"F8.wireOp",EDGE,"E12.5.0"),sQuery(id+"F8.wireOp",EDGE,"E12.5.1"),sQuery(id+"F8.wireOp",EDGE,"E12.6.0"),sQuery(id+"F8.wireOp",EDGE,"E13"),sQuery(id+"F8.wireOp",EDGE,"E14")])]}),"instanceName":"2"}),"instanceName":"2"});
            var Q4;
            Q4=sQuery(id+"F55.wireOp",EDGE,"E55");
            circularPattern(context, id + "F56", {"entities" : qUnion([Q0, Q1, Q2, Q3]), "axis" : qUnion([Q4]), "angle" : 120 * degree, "instanceCount" : 2, "oppositeDirection" : true});
        }
        {
            var Q0;
            Q0=makeQuery(id+"F56.opPattern","COPY",FACE,{"derivedFrom":makeQuery(id+"F26.opPattern","COPY",FACE,{"derivedFrom":makeQuery(id+"F3.opExtrude","CAP_FACE",FACE,{"disambiguationData":[OSD([sQuery(id+"F1.wireOp",EDGE,"E2.0"),sQuery(id+"F1.wireOp",EDGE,"E2.1"),sQuery(id+"F1.wireOp",EDGE,"E2.2"),sQuery(id+"F1.wireOp",EDGE,"E2.3"),sQuery(id+"F1.wireOp",EDGE,"E2.4"),sQuery(id+"F1.wireOp",EDGE,"E2.5")])],"isStart":true}),"instanceName":"2"}),"instanceName":"1"});
            var sketch = newSketch(context, id + "F57", { "sketchPlane" : qUnion([Q0])});
            skLineSegment(sketch, "E56", {"start": v(-34.48, 6) * mm, "end": v(-19.62, 8.02) * mm});
            skSolve(sketch);
        }
        {
            var Q0;
            Q0=sQuery(id+"F57.wireOp",VERTEX,"E56.start");
            var Q1;
            Q1=sQuery(id+"F57.wireOp",VERTEX,"E56.end");
            var Q2;
            Q2=makeQuery(id+"F56.opPattern","COPY",VERTEX,{"derivedFrom":makeQuery(id+"F26.opPattern","COPY",VERTEX,{"derivedFrom":makeQuery(id+"F3.opExtrude","CAP_VERTEX",VERTEX,{"disambiguationData":[OSD([sQuery(id+"F1.wireOp",EDGE,"E2.2"),sQuery(id+"F1.wireOp",EDGE,"E2.3")])],"isStart":false}),"instanceName":"2"}),"instanceName":"1"});
            cPlane(context, id + "F58", {"entities" : qUnion([Q0, Q1, Q2]), "cplaneType" : CPlaneType.THREE_POINT, "offset" : 150 * mm, "width" : 150 * mm, "height" : 150 * mm});
        }
        {
            var Q0;
            Q0=qCreatedBy(id+"F58.planeOp",FACE);
            var sketch = newSketch(context, id + "F59", { "sketchPlane" : qUnion([Q0])});
            skLineSegment(sketch, "E57.0", {"start": v(-8.72, -69.64) * mm, "end": v(-20.93, -60.93) * mm});
            skLineSegment(sketch, "E58", {"start": v(-20.93, -60.93) * mm, "end": v(-30.12, -73.8) * mm});
            skSolve(sketch);
        }
        {
            var Q0;
            Q0=makeQuery(id+"F52.opPattern","COPY",BODY,{"derivedFrom":makeQuery(id+"F3.opExtrude","SWEPT_BODY",BODY,{"disambiguationData":[OSD([sQuery(id+"F1.wireOp",EDGE,"E2.0"),sQuery(id+"F1.wireOp",EDGE,"E2.1"),sQuery(id+"F1.wireOp",EDGE,"E2.2"),sQuery(id+"F1.wireOp",EDGE,"E2.3"),sQuery(id+"F1.wireOp",EDGE,"E2.4"),sQuery(id+"F1.wireOp",EDGE,"E2.5")])]}),"instanceName":"1"});
            var Q1;
            Q1=makeQuery(id+"F52.opPattern","COPY",BODY,{"derivedFrom":makeQuery(id+"F16.opPattern","COPY",BODY,{"derivedFrom":makeQuery(id+"F15.opPattern","COPY",BODY,{"derivedFrom":makeQuery(id+"F9.opExtrude","SWEPT_BODY",BODY,{"disambiguationData":[OSD([sQuery(id+"F8.wireOp",EDGE,"E7.0"),sQuery(id+"F8.wireOp",EDGE,"E10"),sQuery(id+"F8.wireOp",EDGE,"E11"),sQuery(id+"F8.wireOp",EDGE,"E12.1.0"),sQuery(id+"F8.wireOp",EDGE,"E12.1.1"),sQuery(id+"F8.wireOp",EDGE,"E12.2.0"),sQuery(id+"F8.wireOp",EDGE,"E12.2.1"),sQuery(id+"F8.wireOp",EDGE,"E12.3.0"),sQuery(id+"F8.wireOp",EDGE,"E12.3.1"),sQuery(id+"F8.wireOp",EDGE,"E12.4.0"),sQuery(id+"F8.wireOp",EDGE,"E12.4.1"),sQuery(id+"F8.wireOp",EDGE,"E12.5.0"),sQuery(id+"F8.wireOp",EDGE,"E12.5.1"),sQuery(id+"F8.wireOp",EDGE,"E12.6.0"),sQuery(id+"F8.wireOp",EDGE,"E13"),sQuery(id+"F8.wireOp",EDGE,"E14")])]}),"instanceName":"2"}),"instanceName":"1"}),"instanceName":"1"});
            var Q2;
            Q2=makeQuery(id+"F52.opPattern","COPY",BODY,{"derivedFrom":makeQuery(id+"F16.opPattern","COPY",BODY,{"derivedFrom":makeQuery(id+"F15.opPattern","COPY",BODY,{"derivedFrom":makeQuery(id+"F9.opExtrude","SWEPT_BODY",BODY,{"disambiguationData":[OSD([sQuery(id+"F8.wireOp",EDGE,"E7.0"),sQuery(id+"F8.wireOp",EDGE,"E10"),sQuery(id+"F8.wireOp",EDGE,"E11"),sQuery(id+"F8.wireOp",EDGE,"E12.1.0"),sQuery(id+"F8.wireOp",EDGE,"E12.1.1"),sQuery(id+"F8.wireOp",EDGE,"E12.2.0"),sQuery(id+"F8.wireOp",EDGE,"E12.2.1"),sQuery(id+"F8.wireOp",EDGE,"E12.3.0"),sQuery(id+"F8.wireOp",EDGE,"E12.3.1"),sQuery(id+"F8.wireOp",EDGE,"E12.4.0"),sQuery(id+"F8.wireOp",EDGE,"E12.4.1"),sQuery(id+"F8.wireOp",EDGE,"E12.5.0"),sQuery(id+"F8.wireOp",EDGE,"E12.5.1"),sQuery(id+"F8.wireOp",EDGE,"E12.6.0"),sQuery(id+"F8.wireOp",EDGE,"E13"),sQuery(id+"F8.wireOp",EDGE,"E14")])]}),"instanceName":"1"}),"instanceName":"1"}),"instanceName":"1"});
            var Q3;
            Q3=makeQuery(id+"F52.opPattern","COPY",BODY,{"derivedFrom":makeQuery(id+"F13.opPattern","COPY",BODY,{"derivedFrom":makeQuery(id+"F9.opExtrude","SWEPT_BODY",BODY,{"disambiguationData":[OSD([sQuery(id+"F8.wireOp",EDGE,"E7.0"),sQuery(id+"F8.wireOp",EDGE,"E10"),sQuery(id+"F8.wireOp",EDGE,"E11"),sQuery(id+"F8.wireOp",EDGE,"E12.1.0"),sQuery(id+"F8.wireOp",EDGE,"E12.1.1"),sQuery(id+"F8.wireOp",EDGE,"E12.2.0"),sQuery(id+"F8.wireOp",EDGE,"E12.2.1"),sQuery(id+"F8.wireOp",EDGE,"E12.3.0"),sQuery(id+"F8.wireOp",EDGE,"E12.3.1"),sQuery(id+"F8.wireOp",EDGE,"E12.4.0"),sQuery(id+"F8.wireOp",EDGE,"E12.4.1"),sQuery(id+"F8.wireOp",EDGE,"E12.5.0"),sQuery(id+"F8.wireOp",EDGE,"E12.5.1"),sQuery(id+"F8.wireOp",EDGE,"E12.6.0"),sQuery(id+"F8.wireOp",EDGE,"E13"),sQuery(id+"F8.wireOp",EDGE,"E14")])]}),"instanceName":"1"}),"instanceName":"1"});
            var Q4;
            Q4=sQuery(id+"F59.wireOp",EDGE,"E58");
            circularPattern(context, id + "F60", {"entities" : qUnion([Q0, Q1, Q2, Q3]), "axis" : qUnion([Q4]), "angle" : 120 * degree, "instanceCount" : 2, "oppositeDirection" : true});
        }
        {
            var Q0;
            Q0=makeQuery(id+"F22.opPattern","COPY",BODY,{"derivedFrom":makeQuery(id+"F17.opPattern","COPY",BODY,{"derivedFrom":makeQuery(id+"F16.opPattern","COPY",BODY,{"derivedFrom":makeQuery(id+"F15.opPattern","COPY",BODY,{"derivedFrom":makeQuery(id+"F9.opExtrude","SWEPT_BODY",BODY,{"disambiguationData":[OSD([sQuery(id+"F8.wireOp",EDGE,"E7.0"),sQuery(id+"F8.wireOp",EDGE,"E10"),sQuery(id+"F8.wireOp",EDGE,"E11"),sQuery(id+"F8.wireOp",EDGE,"E12.1.0"),sQuery(id+"F8.wireOp",EDGE,"E12.1.1"),sQuery(id+"F8.wireOp",EDGE,"E12.2.0"),sQuery(id+"F8.wireOp",EDGE,"E12.2.1"),sQuery(id+"F8.wireOp",EDGE,"E12.3.0"),sQuery(id+"F8.wireOp",EDGE,"E12.3.1"),sQuery(id+"F8.wireOp",EDGE,"E12.4.0"),sQuery(id+"F8.wireOp",EDGE,"E12.4.1"),sQuery(id+"F8.wireOp",EDGE,"E12.5.0"),sQuery(id+"F8.wireOp",EDGE,"E12.5.1"),sQuery(id+"F8.wireOp",EDGE,"E12.6.0"),sQuery(id+"F8.wireOp",EDGE,"E13"),sQuery(id+"F8.wireOp",EDGE,"E14")])]}),"instanceName":"1"}),"instanceName":"1"}),"instanceName":"1"}),"instanceName":"1"});
            deleteBodies(context, id + "F61", {"entities" : qUnion([Q0])});
        }
        {
            var Q0;
            Q0=makeQuery(id+"F22.opPattern","COPY",BODY,{"derivedFrom":makeQuery(id+"F17.opPattern","COPY",BODY,{"derivedFrom":makeQuery(id+"F16.opPattern","COPY",BODY,{"derivedFrom":makeQuery(id+"F15.opPattern","COPY",BODY,{"derivedFrom":makeQuery(id+"F9.opExtrude","SWEPT_BODY",BODY,{"disambiguationData":[OSD([sQuery(id+"F8.wireOp",EDGE,"E7.0"),sQuery(id+"F8.wireOp",EDGE,"E10"),sQuery(id+"F8.wireOp",EDGE,"E11"),sQuery(id+"F8.wireOp",EDGE,"E12.1.0"),sQuery(id+"F8.wireOp",EDGE,"E12.1.1"),sQuery(id+"F8.wireOp",EDGE,"E12.2.0"),sQuery(id+"F8.wireOp",EDGE,"E12.2.1"),sQuery(id+"F8.wireOp",EDGE,"E12.3.0"),sQuery(id+"F8.wireOp",EDGE,"E12.3.1"),sQuery(id+"F8.wireOp",EDGE,"E12.4.0"),sQuery(id+"F8.wireOp",EDGE,"E12.4.1"),sQuery(id+"F8.wireOp",EDGE,"E12.5.0"),sQuery(id+"F8.wireOp",EDGE,"E12.5.1"),sQuery(id+"F8.wireOp",EDGE,"E12.6.0"),sQuery(id+"F8.wireOp",EDGE,"E13"),sQuery(id+"F8.wireOp",EDGE,"E14")])]}),"instanceName":"1"}),"instanceName":"1"}),"instanceName":"1"}),"instanceName":"2"});
            deleteBodies(context, id + "F62", {"entities" : qUnion([Q0])});
        }
        {
            var Q0;
            Q0=makeQuery(id+"F26.opPattern","COPY",BODY,{"derivedFrom":makeQuery(id+"F16.opPattern","COPY",BODY,{"derivedFrom":makeQuery(id+"F15.opPattern","COPY",BODY,{"derivedFrom":makeQuery(id+"F9.opExtrude","SWEPT_BODY",BODY,{"disambiguationData":[OSD([sQuery(id+"F8.wireOp",EDGE,"E7.0"),sQuery(id+"F8.wireOp",EDGE,"E10"),sQuery(id+"F8.wireOp",EDGE,"E11"),sQuery(id+"F8.wireOp",EDGE,"E12.1.0"),sQuery(id+"F8.wireOp",EDGE,"E12.1.1"),sQuery(id+"F8.wireOp",EDGE,"E12.2.0"),sQuery(id+"F8.wireOp",EDGE,"E12.2.1"),sQuery(id+"F8.wireOp",EDGE,"E12.3.0"),sQuery(id+"F8.wireOp",EDGE,"E12.3.1"),sQuery(id+"F8.wireOp",EDGE,"E12.4.0"),sQuery(id+"F8.wireOp",EDGE,"E12.4.1"),sQuery(id+"F8.wireOp",EDGE,"E12.5.0"),sQuery(id+"F8.wireOp",EDGE,"E12.5.1"),sQuery(id+"F8.wireOp",EDGE,"E12.6.0"),sQuery(id+"F8.wireOp",EDGE,"E13"),sQuery(id+"F8.wireOp",EDGE,"E14")])]}),"instanceName":"1"}),"instanceName":"1"}),"instanceName":"1"});
            deleteBodies(context, id + "F63", {"entities" : qUnion([Q0])});
        }
        {
            var Q0;
            Q0=makeQuery(id+"F26.opPattern","COPY",BODY,{"derivedFrom":makeQuery(id+"F16.opPattern","COPY",BODY,{"derivedFrom":makeQuery(id+"F15.opPattern","COPY",BODY,{"derivedFrom":makeQuery(id+"F9.opExtrude","SWEPT_BODY",BODY,{"disambiguationData":[OSD([sQuery(id+"F8.wireOp",EDGE,"E7.0"),sQuery(id+"F8.wireOp",EDGE,"E10"),sQuery(id+"F8.wireOp",EDGE,"E11"),sQuery(id+"F8.wireOp",EDGE,"E12.1.0"),sQuery(id+"F8.wireOp",EDGE,"E12.1.1"),sQuery(id+"F8.wireOp",EDGE,"E12.2.0"),sQuery(id+"F8.wireOp",EDGE,"E12.2.1"),sQuery(id+"F8.wireOp",EDGE,"E12.3.0"),sQuery(id+"F8.wireOp",EDGE,"E12.3.1"),sQuery(id+"F8.wireOp",EDGE,"E12.4.0"),sQuery(id+"F8.wireOp",EDGE,"E12.4.1"),sQuery(id+"F8.wireOp",EDGE,"E12.5.0"),sQuery(id+"F8.wireOp",EDGE,"E12.5.1"),sQuery(id+"F8.wireOp",EDGE,"E12.6.0"),sQuery(id+"F8.wireOp",EDGE,"E13"),sQuery(id+"F8.wireOp",EDGE,"E14")])]}),"instanceName":"1"}),"instanceName":"1"}),"instanceName":"2"});
            deleteBodies(context, id + "F64", {"entities" : qUnion([Q0])});
        }
        {
            var Q0;
            Q0=makeQuery(id+"F9.opExtrude","SWEPT_BODY",BODY,{"disambiguationData":[OSD([sQuery(id+"F8.wireOp",EDGE,"E7.0"),sQuery(id+"F8.wireOp",EDGE,"E10"),sQuery(id+"F8.wireOp",EDGE,"E11"),sQuery(id+"F8.wireOp",EDGE,"E12.1.0"),sQuery(id+"F8.wireOp",EDGE,"E12.1.1"),sQuery(id+"F8.wireOp",EDGE,"E12.2.0"),sQuery(id+"F8.wireOp",EDGE,"E12.2.1"),sQuery(id+"F8.wireOp",EDGE,"E12.3.0"),sQuery(id+"F8.wireOp",EDGE,"E12.3.1"),sQuery(id+"F8.wireOp",EDGE,"E12.4.0"),sQuery(id+"F8.wireOp",EDGE,"E12.4.1"),sQuery(id+"F8.wireOp",EDGE,"E12.5.0"),sQuery(id+"F8.wireOp",EDGE,"E12.5.1"),sQuery(id+"F8.wireOp",EDGE,"E12.6.0"),sQuery(id+"F8.wireOp",EDGE,"E13"),sQuery(id+"F8.wireOp",EDGE,"E14")])]});
            var Q1;
            Q1=makeQuery(id+"F13.opPattern","COPY",BODY,{"derivedFrom":makeQuery(id+"F9.opExtrude","SWEPT_BODY",BODY,{"disambiguationData":[OSD([sQuery(id+"F8.wireOp",EDGE,"E7.0"),sQuery(id+"F8.wireOp",EDGE,"E10"),sQuery(id+"F8.wireOp",EDGE,"E11"),sQuery(id+"F8.wireOp",EDGE,"E12.1.0"),sQuery(id+"F8.wireOp",EDGE,"E12.1.1"),sQuery(id+"F8.wireOp",EDGE,"E12.2.0"),sQuery(id+"F8.wireOp",EDGE,"E12.2.1"),sQuery(id+"F8.wireOp",EDGE,"E12.3.0"),sQuery(id+"F8.wireOp",EDGE,"E12.3.1"),sQuery(id+"F8.wireOp",EDGE,"E12.4.0"),sQuery(id+"F8.wireOp",EDGE,"E12.4.1"),sQuery(id+"F8.wireOp",EDGE,"E12.5.0"),sQuery(id+"F8.wireOp",EDGE,"E12.5.1"),sQuery(id+"F8.wireOp",EDGE,"E12.6.0"),sQuery(id+"F8.wireOp",EDGE,"E13"),sQuery(id+"F8.wireOp",EDGE,"E14")])]}),"instanceName":"1"});
            var Q2;
            Q2=makeQuery(id+"F16.opPattern","COPY",BODY,{"derivedFrom":makeQuery(id+"F15.opPattern","COPY",BODY,{"derivedFrom":makeQuery(id+"F9.opExtrude","SWEPT_BODY",BODY,{"disambiguationData":[OSD([sQuery(id+"F8.wireOp",EDGE,"E7.0"),sQuery(id+"F8.wireOp",EDGE,"E10"),sQuery(id+"F8.wireOp",EDGE,"E11"),sQuery(id+"F8.wireOp",EDGE,"E12.1.0"),sQuery(id+"F8.wireOp",EDGE,"E12.1.1"),sQuery(id+"F8.wireOp",EDGE,"E12.2.0"),sQuery(id+"F8.wireOp",EDGE,"E12.2.1"),sQuery(id+"F8.wireOp",EDGE,"E12.3.0"),sQuery(id+"F8.wireOp",EDGE,"E12.3.1"),sQuery(id+"F8.wireOp",EDGE,"E12.4.0"),sQuery(id+"F8.wireOp",EDGE,"E12.4.1"),sQuery(id+"F8.wireOp",EDGE,"E12.5.0"),sQuery(id+"F8.wireOp",EDGE,"E12.5.1"),sQuery(id+"F8.wireOp",EDGE,"E12.6.0"),sQuery(id+"F8.wireOp",EDGE,"E13"),sQuery(id+"F8.wireOp",EDGE,"E14")])]}),"instanceName":"1"}),"instanceName":"4"});
            var Q3;
            Q3=makeQuery(id+"F44.opPattern","COPY",BODY,{"derivedFrom":makeQuery(id+"F40.opPattern","COPY",BODY,{"derivedFrom":makeQuery(id+"F22.opPattern","COPY",BODY,{"derivedFrom":makeQuery(id+"F17.opPattern","COPY",BODY,{"derivedFrom":makeQuery(id+"F13.opPattern","COPY",BODY,{"derivedFrom":makeQuery(id+"F9.opExtrude","SWEPT_BODY",BODY,{"disambiguationData":[OSD([sQuery(id+"F8.wireOp",EDGE,"E7.0"),sQuery(id+"F8.wireOp",EDGE,"E10"),sQuery(id+"F8.wireOp",EDGE,"E11"),sQuery(id+"F8.wireOp",EDGE,"E12.1.0"),sQuery(id+"F8.wireOp",EDGE,"E12.1.1"),sQuery(id+"F8.wireOp",EDGE,"E12.2.0"),sQuery(id+"F8.wireOp",EDGE,"E12.2.1"),sQuery(id+"F8.wireOp",EDGE,"E12.3.0"),sQuery(id+"F8.wireOp",EDGE,"E12.3.1"),sQuery(id+"F8.wireOp",EDGE,"E12.4.0"),sQuery(id+"F8.wireOp",EDGE,"E12.4.1"),sQuery(id+"F8.wireOp",EDGE,"E12.5.0"),sQuery(id+"F8.wireOp",EDGE,"E12.5.1"),sQuery(id+"F8.wireOp",EDGE,"E12.6.0"),sQuery(id+"F8.wireOp",EDGE,"E13"),sQuery(id+"F8.wireOp",EDGE,"E14")])]}),"instanceName":"1"}),"instanceName":"1"}),"instanceName":"2"}),"instanceName":"2"}),"instanceName":"2"});
            var Q4;
            Q4=makeQuery(id+"F60.opPattern","COPY",BODY,{"derivedFrom":makeQuery(id+"F52.opPattern","COPY",BODY,{"derivedFrom":makeQuery(id+"F16.opPattern","COPY",BODY,{"derivedFrom":makeQuery(id+"F15.opPattern","COPY",BODY,{"derivedFrom":makeQuery(id+"F9.opExtrude","SWEPT_BODY",BODY,{"disambiguationData":[OSD([sQuery(id+"F8.wireOp",EDGE,"E7.0"),sQuery(id+"F8.wireOp",EDGE,"E10"),sQuery(id+"F8.wireOp",EDGE,"E11"),sQuery(id+"F8.wireOp",EDGE,"E12.1.0"),sQuery(id+"F8.wireOp",EDGE,"E12.1.1"),sQuery(id+"F8.wireOp",EDGE,"E12.2.0"),sQuery(id+"F8.wireOp",EDGE,"E12.2.1"),sQuery(id+"F8.wireOp",EDGE,"E12.3.0"),sQuery(id+"F8.wireOp",EDGE,"E12.3.1"),sQuery(id+"F8.wireOp",EDGE,"E12.4.0"),sQuery(id+"F8.wireOp",EDGE,"E12.4.1"),sQuery(id+"F8.wireOp",EDGE,"E12.5.0"),sQuery(id+"F8.wireOp",EDGE,"E12.5.1"),sQuery(id+"F8.wireOp",EDGE,"E12.6.0"),sQuery(id+"F8.wireOp",EDGE,"E13"),sQuery(id+"F8.wireOp",EDGE,"E14")])]}),"instanceName":"1"}),"instanceName":"1"}),"instanceName":"1"}),"instanceName":"1"});
            var Q5;
            Q5=makeQuery(id+"F18.opPattern","COPY",BODY,{"derivedFrom":makeQuery(id+"F13.opPattern","COPY",BODY,{"derivedFrom":makeQuery(id+"F9.opExtrude","SWEPT_BODY",BODY,{"disambiguationData":[OSD([sQuery(id+"F8.wireOp",EDGE,"E7.0"),sQuery(id+"F8.wireOp",EDGE,"E10"),sQuery(id+"F8.wireOp",EDGE,"E11"),sQuery(id+"F8.wireOp",EDGE,"E12.1.0"),sQuery(id+"F8.wireOp",EDGE,"E12.1.1"),sQuery(id+"F8.wireOp",EDGE,"E12.2.0"),sQuery(id+"F8.wireOp",EDGE,"E12.2.1"),sQuery(id+"F8.wireOp",EDGE,"E12.3.0"),sQuery(id+"F8.wireOp",EDGE,"E12.3.1"),sQuery(id+"F8.wireOp",EDGE,"E12.4.0"),sQuery(id+"F8.wireOp",EDGE,"E12.4.1"),sQuery(id+"F8.wireOp",EDGE,"E12.5.0"),sQuery(id+"F8.wireOp",EDGE,"E12.5.1"),sQuery(id+"F8.wireOp",EDGE,"E12.6.0"),sQuery(id+"F8.wireOp",EDGE,"E13"),sQuery(id+"F8.wireOp",EDGE,"E14")])]}),"instanceName":"3"}),"instanceName":"1"});
            var Q6;
            Q6=makeQuery(id+"F44.opPattern","COPY",BODY,{"derivedFrom":makeQuery(id+"F40.opPattern","COPY",BODY,{"derivedFrom":makeQuery(id+"F18.opPattern","COPY",BODY,{"derivedFrom":makeQuery(id+"F13.opPattern","COPY",BODY,{"derivedFrom":makeQuery(id+"F9.opExtrude","SWEPT_BODY",BODY,{"disambiguationData":[OSD([sQuery(id+"F8.wireOp",EDGE,"E7.0"),sQuery(id+"F8.wireOp",EDGE,"E10"),sQuery(id+"F8.wireOp",EDGE,"E11"),sQuery(id+"F8.wireOp",EDGE,"E12.1.0"),sQuery(id+"F8.wireOp",EDGE,"E12.1.1"),sQuery(id+"F8.wireOp",EDGE,"E12.2.0"),sQuery(id+"F8.wireOp",EDGE,"E12.2.1"),sQuery(id+"F8.wireOp",EDGE,"E12.3.0"),sQuery(id+"F8.wireOp",EDGE,"E12.3.1"),sQuery(id+"F8.wireOp",EDGE,"E12.4.0"),sQuery(id+"F8.wireOp",EDGE,"E12.4.1"),sQuery(id+"F8.wireOp",EDGE,"E12.5.0"),sQuery(id+"F8.wireOp",EDGE,"E12.5.1"),sQuery(id+"F8.wireOp",EDGE,"E12.6.0"),sQuery(id+"F8.wireOp",EDGE,"E13"),sQuery(id+"F8.wireOp",EDGE,"E14")])]}),"instanceName":"2"}),"instanceName":"1"}),"instanceName":"2"}),"instanceName":"1"});
            transform(context, id + "F65", {"entities" : qUnion([Q0, Q1, Q2, Q3, Q4, Q5, Q6]), "transformType" : TransformType.TRANSLATION_3D, "dx" : -36 * mm, "dy" : -74.6 * mm, "dz" : 0 * mm, "makeCopy" : false});
        }
    });
